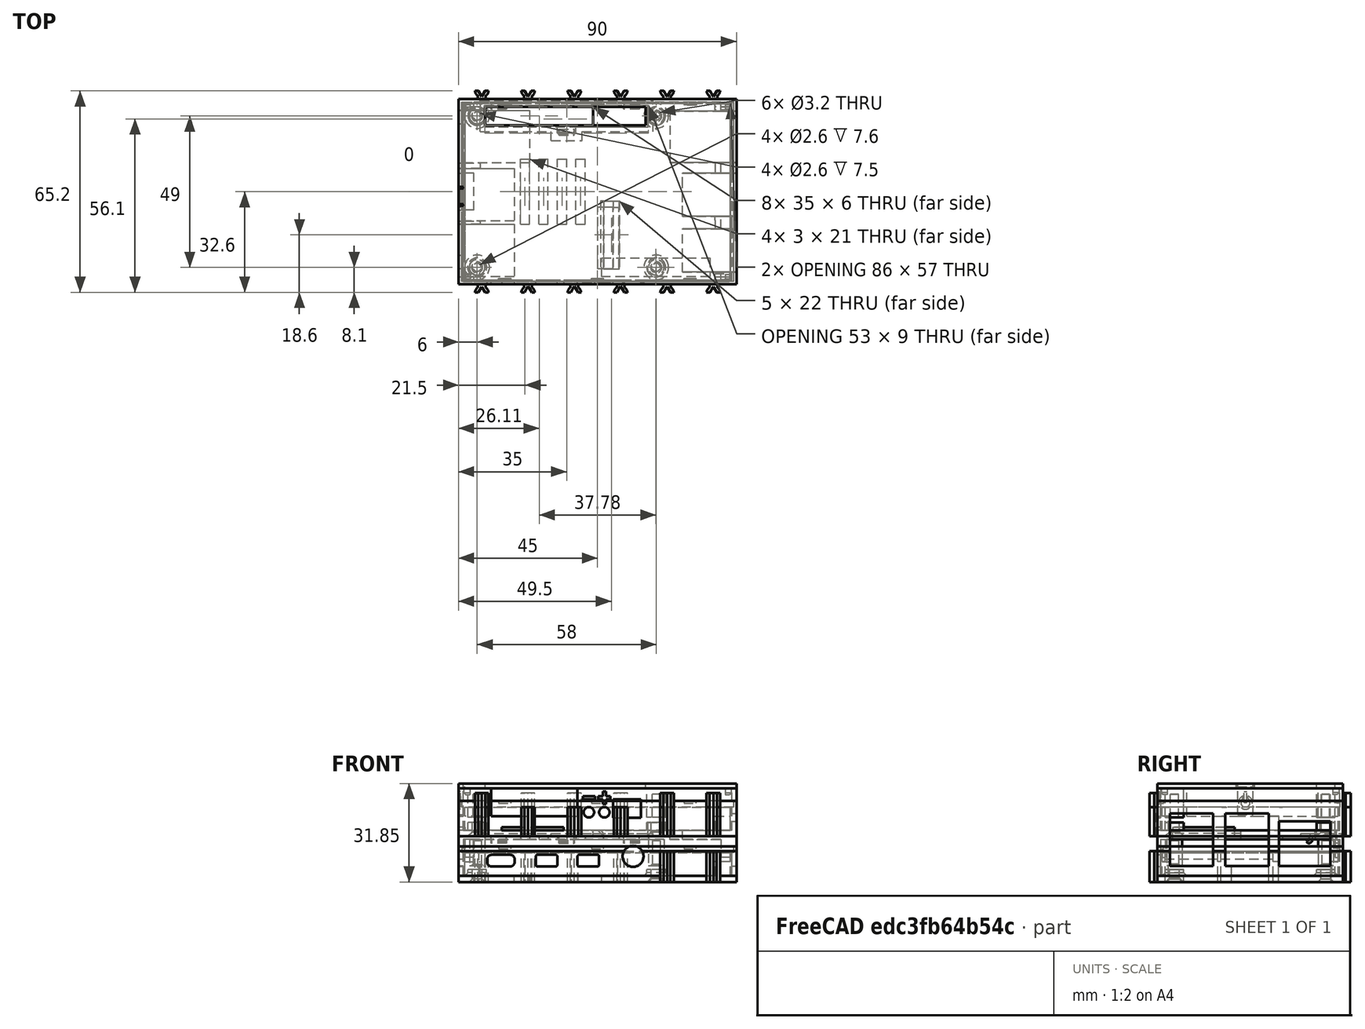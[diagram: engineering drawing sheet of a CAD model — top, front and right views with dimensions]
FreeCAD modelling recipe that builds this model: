
FCSTD DOCUMENT  (FreeCAD 0.19RUnknown)
Label: TX-Pi4_Case
License: All rights reserved
LicenseURL: http://en.wikipedia.org/wiki/All_rights_reserved
objects: Part::Box×86, Part::MultiFuse×79, Part::Cylinder×47, Part::Cut×28, Part::Extrusion×17, Sketcher::SketchObject×17, Part::Chamfer×16, Part::RegularPolygon×8, PartDesign::Pad×7, Part::Fillet×3, Part::Feature×1, PartDesign::Pocket×1, PartDesign::LinearPattern×1, PartDesign::Chamfer×1
note: 321 computed .brp shape members not serialized (recipe doc carries the construction recipe); baked Part::Feature solids carry a one-line shape summary decoded from their .brp

FEATURE [Part::Feature] RPi_4_dummy001
  Placement = pos=(-10,0,0) rot=(0,0,1;0rad)
  shape: bbox 90.5 x 58.5 x 18.2 mm, 1420 faces, 0 solids (baked)
FEATURE [Part::Box] Box  label="Aussen"
  AttacherType = Attacher::AttachEngine3D
  Height = 10
  Length = 90
  Placement = pos=(-45,-30,0) rot=(0,0,1;0rad)
  Width = 60
FEATURE [Part::Cylinder] Cylinder008  label="Audio"
  Angle = 360
  AttacherType = Attacher::AttachEngine3D
  Height = 10
  Placement = pos=(11.5,-23,8) rot=(1,0,0;1.5708rad)
  Radius = 3.4
FEATURE [Part::Cylinder] Cylinder001  label="Zylinder001"
  Angle = 360
  AttacherType = Attacher::AttachEngine3D
  Height = 10
  Placement = pos=(19,24.5,0) rot=(0,0,1;0rad)
  Radius = 1.6
FEATURE [Part::Box] Box001  label="Innen"
  AttacherType = Attacher::AttachEngine3D
  Height = 9.75
  Length = 87
  Placement = pos=(-43.5,-29,2) rot=(0,0,1;0rad)
  Width = 58
FEATURE [Part::Cylinder] Cylinder002  label="Zylinder002"
  Angle = 360
  AttacherType = Attacher::AttachEngine3D
  Height = 10
  Placement = pos=(19,24.5,0) rot=(0,0,1;0rad)
  Radius = 1.6
FEATURE [Part::Cut] Cut  label="Wanne roh"
  Base = -> Box
  Tool = -> Box001
FEATURE [Part::Cylinder] Cylinder  label="Zylinder"
  Angle = 360
  AttacherType = Attacher::AttachEngine3D
  Height = 10
  Placement = pos=(19,-24.5,0) rot=(0,0,1;0rad)
  Radius = 1.6
FEATURE [Part::MultiFuse] Fusion
  Shapes = -> [Cylinder,Cylinder001]
FEATURE [Part::Cylinder] Cylinder004  label="Zylinder004"
  Angle = 360
  AttacherType = Attacher::AttachEngine3D
  Height = 2
  Placement = pos=(19,24.5,0) rot=(0,0,1;0rad)
  Radius = 3
FEATURE [Part::Cylinder] Cylinder005  label="Zylinder005"
  Angle = 360
  AttacherType = Attacher::AttachEngine3D
  Height = 2
  Placement = pos=(19,24.5,0) rot=(0,0,1;0rad)
  Radius = 3
FEATURE [Part::Cylinder] Cylinder006  label="Zylinder006"
  Angle = 360
  AttacherType = Attacher::AttachEngine3D
  Height = 2
  Placement = pos=(19,-24.5,0) rot=(0,0,1;0rad)
  Radius = 3
FEATURE [Part::Cylinder] Cylinder003  label="Zylinder003"
  Angle = 360
  AttacherType = Attacher::AttachEngine3D
  Height = 10
  Placement = pos=(19,-24.5,0) rot=(0,0,1;0rad)
  Radius = 1.6
FEATURE [Part::MultiFuse] Fusion001
  Placement = pos=(-58,0,0) rot=(0,0,1;0rad)
  Shapes = -> [Cylinder003,Cylinder002]
FEATURE [Part::MultiFuse] Fusion002  label="Bohrungen"
  Placement = pos=(0,0,-5.3) rot=(0,0,1;0rad)
  Shapes = -> [Fusion001,Fusion]
FEATURE [Part::MultiFuse] Fusion003
  Shapes = -> [Cylinder006,Cylinder004]
FEATURE [Part::Cylinder] Cylinder007  label="Zylinder007"
  Angle = 360
  AttacherType = Attacher::AttachEngine3D
  Height = 2
  Placement = pos=(19,-24.5,0) rot=(0,0,1;0rad)
  Radius = 3
FEATURE [Part::MultiFuse] Fusion005
  Placement = pos=(-58,0,0) rot=(0,0,1;0rad)
  Shapes = -> [Cylinder007,Cylinder005]
FEATURE [Part::MultiFuse] Fusion004  label="Stützen"
  Placement = pos=(0,0,2) rot=(0,0,1;0rad)
  Shapes = -> [Fusion005,Fusion003]
FEATURE [Part::Box] Box002  label="SD-Slot"
  AttacherType = Attacher::AttachEngine3D
  Height = 6
  Length = 5
  Placement = pos=(-45,-6,-1) rot=(0,0,1;0rad)
  Width = 12
FEATURE [Part::Box] Box007  label="USB1"
  AttacherType = Attacher::AttachEngine3D
  Height = 16.6
  Length = 22
  Placement = pos=(27.5,-8,4.8) rot=(0,0,1;0rad)
  Width = 14
FEATURE [Part::Box] Box008  label="USB2"
  AttacherType = Attacher::AttachEngine3D
  Height = 16.6
  Length = 22
  Placement = pos=(27.5,-26,4.8) rot=(0,0,1;0rad)
  Width = 14
FEATURE [Part::Box] Box004  label="Würfel001"
  AttacherType = Attacher::AttachEngine3D
  Height = 3.8
  Length = 7
  Placement = pos=(-20,-29,4.7) rot=(0,0,1;0rad)
  Width = 10
FEATURE [Part::Box] Box006  label="Network"
  AttacherType = Attacher::AttachEngine3D
  Height = 14
  Length = 26
  Placement = pos=(23.5,9.4,4.8) rot=(0,0,1;0rad)
  Width = 16.6
FEATURE [Part::Box] Box005  label="Würfel002"
  AttacherType = Attacher::AttachEngine3D
  Height = 3.8
  Length = 7
  Placement = pos=(-20,-29,4.7) rot=(0,0,1;0rad)
  Width = 10
FEATURE [Part::Fillet] Fillet002  label="HDMI-2"
  Base = -> Box005
  Edges = 4 edges r=0.6: [Edge2,Edge4,Edge6,Edge8]
  Placement = pos=(13.5,-4,0) rot=(0,0,1;0rad)
FEATURE [Part::Box] Box003  label="Würfel"
  AttacherType = Attacher::AttachEngine3D
  Height = 3.8
  Length = 9
  Placement = pos=(-35.8,-29,4.7) rot=(0,0,1;0rad)
  Width = 10
FEATURE [Part::Fillet] Fillet  label="USB-C"
  Base = -> Box003
  Edges = 4 edges r=1.6: [Edge2,Edge4,Edge6,Edge8]
  Placement = pos=(0,-4,0) rot=(0,0,1;0rad)
FEATURE [Part::MultiFuse] Fusion007  label="Wanne mit Stuetzen"
  Shapes = -> [Cut,Fusion004]
FEATURE [Part::Fillet] Fillet001  label="HDMI-1"
  Base = -> Box004
  Edges = 4 edges r=0.6: [Edge2,Edge4,Edge6,Edge8]
  Placement = pos=(0,-4,0) rot=(0,0,1;0rad)
FEATURE [Part::MultiFuse] Fusion006  label="Aussparungen"
  Placement = pos=(0,0,0.3) rot=(0,0,1;0rad)
  Shapes = -> [Fusion002,Box002,Fillet,Fillet001,Fillet002,Cylinder008,Box006,Box007,Box008]
FEATURE [Part::Cut] Cut001  label="Wanne mit Aussparungen"
  Base = -> Fusion007
  Tool = -> Fusion006
FEATURE [Part::Chamfer] Chamfer002  label="Wanne Fasen innen"
  Base = -> Cut001
  Edges = 4 edges r=1: [Edge137,Edge138,Edge139,Edge140]
FEATURE [Part::Chamfer] Chamfer003  label="Wanne Fasen aussen"
  Base = -> Chamfer002
  Edges = 4 edges: [Edge96 r=1,Edge97 r=1.3,Edge98 r=1,Edge99 r=1]
FEATURE [Part::Box] Box026  label="Würfel017"
  AttacherType = Attacher::AttachEngine3D
  Height = 10
  Length = 5
  Placement = pos=(-40,-37.6,-3) rot=(0,0,1;0rad)
  Width = 5
FEATURE [Part::Box] Box035  label="Würfel026"
  AttacherType = Attacher::AttachEngine3D
  Height = 10
  Length = 2.5
  Placement = pos=(-38.75,-32.6,-3) rot=(0,0,1;0rad)
  Width = 2.6
FEATURE [Part::RegularPolygon] RegularPolygon005  label="Regelmäßiges Polygon005"
  AttacherType = Attacher::AttachEngine3D
  Circumradius = 2
  Placement = pos=(0,0,0) rot=(0,0,1;1.5708rad)
  Polygon = 3
FEATURE [Part::Cylinder] Cylinder018  label="Zylinder017"
  Angle = 360
  AttacherType = Attacher::AttachEngine3D
  Height = 10
  Placement = pos=(-37.5,-32.8,-3) rot=(0,0,1;0rad)
  Radius = 2.2
FEATURE [Part::Box] Box034  label="Würfel025"
  AttacherType = Attacher::AttachEngine3D
  Height = 10
  Length = 5
  Placement = pos=(-40,-37.6,-3) rot=(0,0,1;0rad)
  Width = 5
FEATURE [Part::Box] Box010  label="Würfel004"
  AttacherType = Attacher::AttachEngine3D
  Height = 3
  Length = 3
  Placement = pos=(10,-10.5,0) rot=(0,0,1;0rad)
  Width = 21
FEATURE [Part::Box] Box011  label="Deckel innen a"
  AttacherType = Attacher::AttachEngine3D
  Height = 10
  Length = 80
  Placement = pos=(-40,-29,1) rot=(0,0,1;0rad)
  Width = 58
FEATURE [Part::Cylinder] Cylinder012  label="Zylinder011"
  Angle = 360
  AttacherType = Attacher::AttachEngine3D
  Height = 8.5
  Placement = pos=(-19,24.5,1) rot=(0,0,1;0rad)
  Radius = 1.3
FEATURE [Part::Box] Box022  label="Würfel013"
  AttacherType = Attacher::AttachEngine3D
  Height = 10
  Length = 2.5
  Placement = pos=(-38.75,-32.6,-3) rot=(0,0,1;0rad)
  Width = 2.6
FEATURE [Part::Cylinder] Cylinder015  label="Zylinder014"
  Angle = 360
  AttacherType = Attacher::AttachEngine3D
  Height = 8.5
  Placement = pos=(-19,-24.5,1) rot=(0,0,1;0rad)
  Radius = 1.3
FEATURE [Part::Cylinder] Cylinder024  label="Zylinder023"
  Angle = 360
  AttacherType = Attacher::AttachEngine3D
  Height = 10
  Placement = pos=(-37.5,-32.8,-3) rot=(0,0,1;0rad)
  Radius = 2.2
FEATURE [Part::Cylinder] Cylinder013  label="Zylinder012"
  Angle = 360
  AttacherType = Attacher::AttachEngine3D
  Height = 8.5
  Placement = pos=(39,24.5,1) rot=(0,0,1;0rad)
  Radius = 1.3
FEATURE [Part::Cylinder] Cylinder016  label="Zylinder015"
  Angle = 360
  AttacherType = Attacher::AttachEngine3D
  Height = 8.5
  Placement = pos=(39,-24.5,1) rot=(0,0,1;0rad)
  Radius = 1.3
FEATURE [Part::Box] Box027  label="Würfel018"
  AttacherType = Attacher::AttachEngine3D
  Height = 10
  Length = 2.5
  Placement = pos=(-38.75,-32.6,-3) rot=(0,0,1;0rad)
  Width = 2.6
FEATURE [Part::MultiFuse] Fusion009  label="Schraubenbohrungen"
  Placement = pos=(0,0,0.4) rot=(0,0,1;0rad)
  Shapes = -> [Cylinder012,Cylinder013,Cylinder015,Cylinder016]
FEATURE [Part::Cylinder] Cylinder011  label="Zylinder010"
  Angle = 360
  AttacherType = Attacher::AttachEngine3D
  Height = 8.5
  Placement = pos=(-19,24.5,1) rot=(0,0,1;0rad)
  Radius = 2.5
FEATURE [Part::Box] Box021  label="Würfel012"
  AttacherType = Attacher::AttachEngine3D
  Height = 10
  Length = 53
  Placement = pos=(-16.5,21,0) rot=(0,0,1;0rad)
  Width = 7
FEATURE [Part::Box] Box018  label="Würfel005"
  AttacherType = Attacher::AttachEngine3D
  Height = 6.75
  Length = 3
  Placement = pos=(40,27.5,0) rot=(0,0,1;0rad)
  Width = 1
FEATURE [Part::Cylinder] Cylinder010  label="Zylinder009"
  Angle = 360
  AttacherType = Attacher::AttachEngine3D
  Height = 8.5
  Placement = pos=(39,-24.5,1) rot=(0,0,1;0rad)
  Radius = 2.5
FEATURE [Part::Box] Box009  label="Würfel003"
  AttacherType = Attacher::AttachEngine3D
  Height = 3
  Length = 3
  Placement = pos=(4,-10.5,0) rot=(0,0,1;0rad)
  Width = 21
FEATURE [Part::Box] Box013  label="Würfel007"
  AttacherType = Attacher::AttachEngine3D
  Height = 6.75
  Length = 3
  Placement = pos=(40,-28.5,0) rot=(0,0,1;0rad)
  Width = 1
FEATURE [Part::Cylinder] Cylinder009  label="Zylinder008"
  Angle = 360
  AttacherType = Attacher::AttachEngine3D
  Height = 8.5
  Placement = pos=(-19,-24.5,1) rot=(0,0,1;0rad)
  Radius = 2.5
FEATURE [Part::Box] Box017  label="Würfel011"
  AttacherType = Attacher::AttachEngine3D
  Height = 3
  Length = 3
  Placement = pos=(16,-10.5,0) rot=(0,0,1;0rad)
  Width = 21
FEATURE [Part::Box] Box019  label="Deckel aussen"
  AttacherType = Attacher::AttachEngine3D
  Height = 4.75
  Length = 90
  Placement = pos=(-45,-30,0) rot=(0,0,1;0rad)
  Width = 60
FEATURE [Part::Box] Box012  label="Würfel006"
  AttacherType = Attacher::AttachEngine3D
  Height = 6.75
  Length = 3
  Placement = pos=(-43,27.5,0) rot=(0,0,1;0rad)
  Width = 1
FEATURE [Part::Box] Box016  label="Würfel010"
  AttacherType = Attacher::AttachEngine3D
  Height = 3
  Length = 3
  Placement = pos=(22,-10.5,0) rot=(0,0,1;0rad)
  Width = 21
FEATURE [Part::MultiFuse] Fusion010  label="Lueftung"
  Shapes = -> [Box010,Box017,Box009,Box016]
FEATURE [Part::Box] Box015  label="Würfel009"
  AttacherType = Attacher::AttachEngine3D
  Height = 6.75
  Length = 3
  Placement = pos=(-43,-28.5,0) rot=(0,0,1;0rad)
  Width = 1
FEATURE [Part::MultiFuse] Fusion012  label="Zentrierung"
  Shapes = -> [Box015,Box018,Box012,Box013]
FEATURE [Part::Cylinder] Cylinder014  label="Zylinder013"
  Angle = 360
  AttacherType = Attacher::AttachEngine3D
  Height = 8.5
  Placement = pos=(39,24.5,1) rot=(0,0,1;0rad)
  Radius = 2.5
FEATURE [Part::MultiFuse] Fusion008  label="Stuetzen"
  Shapes = -> [Cylinder011,Cylinder014,Cylinder009,Cylinder010]
FEATURE [Part::Box] Box014  label="Würfel008"
  AttacherType = Attacher::AttachEngine3D
  Height = 10
  Length = 6
  Placement = pos=(7,19,0) rot=(0,0,1;0rad)
  Width = 2
FEATURE [Part::Box] Box020  label="Deckel innen b"
  AttacherType = Attacher::AttachEngine3D
  Height = 10
  Length = 3.5
  Placement = pos=(40,-27.5,1) rot=(0,0,1;0rad)
  Width = 56
FEATURE [Part::MultiFuse] Fusion015  label="Deckel innen"
  Shapes = -> [Box011,Box020]
FEATURE [Part::Cut] Cut002  label="Deckel roh"
  Base = -> Box019
  Tool = -> Fusion015
FEATURE [Part::MultiFuse] Fusion013  label="Deckel mit Einbauten"
  Shapes = -> [Cut002,Fusion012,Fusion008]
FEATURE [Part::MultiFuse] Fusion011  label="GPIO-Leiste"
  Shapes = -> [Box014,Box021]
FEATURE [Part::MultiFuse] Fusion014  label="Deckelaussparungen 1"
  Shapes = -> [Fusion009,Fusion010,Fusion011]
FEATURE [Part::Cut] Cut003  label="Deckel mit Aussparungen 1"
  Base = -> Fusion013
  Placement = pos=(0,0,14.75) rot=(0,1,0;3.14159rad)
  Tool = -> Fusion014
FEATURE [Part::Cut] Cut004  label="Deckel mit Aussparungen 2"
  Base = -> Cut003
  Tool = -> Fusion006
FEATURE [Part::RegularPolygon] RegularPolygon006  label="Regelmäßiges Polygon006"
  AttacherType = Attacher::AttachEngine3D
  Circumradius = 2
  Placement = pos=(0,0,0) rot=(0,0,1;1.5708rad)
  Polygon = 3
FEATURE [Part::Box] Box037  label="Würfel028"
  AttacherType = Attacher::AttachEngine3D
  Height = 10
  Length = 5
  Placement = pos=(-40,-37.6,-3) rot=(0,0,1;0rad)
  Width = 5
FEATURE [Part::Box] Box033  label="Würfel024"
  AttacherType = Attacher::AttachEngine3D
  Height = 10
  Length = 2.5
  Placement = pos=(-38.75,-32.6,-3) rot=(0,0,1;0rad)
  Width = 2.6
FEATURE [Part::Box] Box025  label="Würfel016"
  AttacherType = Attacher::AttachEngine3D
  Height = 10
  Length = 5
  Placement = pos=(-40,-37.6,-3) rot=(0,0,1;0rad)
  Width = 5
FEATURE [Part::Box] Box032  label="Würfel023"
  AttacherType = Attacher::AttachEngine3D
  Height = 10
  Length = 5
  Placement = pos=(-40,-37.6,-3) rot=(0,0,1;0rad)
  Width = 5
FEATURE [Part::Box] Box030  label="Würfel021"
  AttacherType = Attacher::AttachEngine3D
  Height = 10
  Length = 5
  Placement = pos=(-40,-37.6,-3) rot=(0,0,1;0rad)
  Width = 5
FEATURE [Part::Cylinder] Cylinder021  label="Zylinder020"
  Angle = 360
  AttacherType = Attacher::AttachEngine3D
  Height = 10
  Placement = pos=(-37.5,-32.8,-3) rot=(0,0,1;0rad)
  Radius = 2.2
FEATURE [Part::RegularPolygon] RegularPolygon  label="Regelmäßiges Polygon"
  AttacherType = Attacher::AttachEngine3D
  Circumradius = 2
  Placement = pos=(0,0,0) rot=(0,0,1;1.5708rad)
  Polygon = 3
FEATURE [Part::Extrusion] Extrude
  Base = -> RegularPolygon
  Dir = (0,0,1)
  DirMode = 2
  FaceMakerClass = Part::FaceMakerBullseye
  LengthFwd = 10
  LengthRev = 0
  Placement = pos=(-37.5,-32.8,-3) rot=(0,0,1;0rad)
  Solid = true
  Symmetric = false
FEATURE [Part::Cylinder] Cylinder023  label="Zylinder022"
  Angle = 360
  AttacherType = Attacher::AttachEngine3D
  Height = 10
  Placement = pos=(-37.5,-32.8,-3) rot=(0,0,1;0rad)
  Radius = 2.2
FEATURE [Part::MultiFuse] Fusion028
  Placement = pos=(0,0,3) rot=(0,0,1;0rad)
  Shapes = -> [Cylinder023,Box035]
FEATURE [Part::Box] Box031  label="Würfel022"
  AttacherType = Attacher::AttachEngine3D
  Height = 10
  Length = 2.5
  Placement = pos=(-38.75,-32.6,-3) rot=(0,0,1;0rad)
  Width = 2.6
FEATURE [Part::MultiFuse] Fusion024
  Placement = pos=(0,0,3) rot=(0,0,1;0rad)
  Shapes = -> [Cylinder021,Box031]
FEATURE [Part::Cylinder] Cylinder019  label="Zylinder018"
  Angle = 360
  AttacherType = Attacher::AttachEngine3D
  Height = 10
  Placement = pos=(-37.5,-32.8,-3) rot=(0,0,1;0rad)
  Radius = 2.2
FEATURE [Part::Chamfer] Chamfer004  label="Deckel Fasen"
  Base = -> Cut004
  Edges = 4 edges r=0.5: [Edge269,Edge270,Edge273,Edge274]
FEATURE [Part::Extrusion] Extrude005
  Base = -> RegularPolygon005
  Dir = (0,0,1)
  DirMode = 2
  FaceMakerClass = Part::FaceMakerBullseye
  LengthFwd = 10
  LengthRev = 0
  Placement = pos=(-37.5,-32.8,-3) rot=(0,0,1;0rad)
  Solid = true
  Symmetric = false
FEATURE [Part::RegularPolygon] RegularPolygon002  label="Regelmäßiges Polygon002"
  AttacherType = Attacher::AttachEngine3D
  Circumradius = 2
  Placement = pos=(0,0,0) rot=(0,0,1;1.5708rad)
  Polygon = 3
FEATURE [Part::Extrusion] Extrude002
  Base = -> RegularPolygon002
  Dir = (0,0,1)
  DirMode = 2
  FaceMakerClass = Part::FaceMakerBullseye
  LengthFwd = 10
  LengthRev = 0
  Placement = pos=(-37.5,-32.8,-3) rot=(0,0,1;0rad)
  Solid = true
  Symmetric = false
FEATURE [Part::Box] Box023  label="Würfel014"
  AttacherType = Attacher::AttachEngine3D
  Height = 10
  Length = 5
  Placement = pos=(-40,-37.6,-3) rot=(0,0,1;0rad)
  Width = 5
FEATURE [Part::MultiFuse] Fusion017
  Placement = pos=(0,0,3) rot=(0,0,1;0rad)
  Shapes = -> [Extrude,Box023]
FEATURE [Part::Box] Box024  label="Würfel015"
  AttacherType = Attacher::AttachEngine3D
  Height = 10
  Length = 2.5
  Placement = pos=(-38.75,-32.6,-3) rot=(0,0,1;0rad)
  Width = 2.6
FEATURE [Part::MultiFuse] Fusion019
  Placement = pos=(0,0,3) rot=(0,0,1;0rad)
  Shapes = -> [Cylinder018,Box024]
FEATURE [Part::Box] Box029  label="Würfel020"
  AttacherType = Attacher::AttachEngine3D
  Height = 10
  Length = 2.5
  Placement = pos=(-38.75,-32.6,-3) rot=(0,0,1;0rad)
  Width = 2.6
FEATURE [Part::MultiFuse] Fusion020
  Placement = pos=(0,0,3) rot=(0,0,1;0rad)
  Shapes = -> [Cylinder019,Box027]
FEATURE [Part::Box] Box036  label="Würfel027"
  AttacherType = Attacher::AttachEngine3D
  Height = 10
  Length = 2.5
  Placement = pos=(-38.75,-32.6,-3) rot=(0,0,1;0rad)
  Width = 2.6
FEATURE [Part::RegularPolygon] RegularPolygon004  label="Regelmäßiges Polygon004"
  AttacherType = Attacher::AttachEngine3D
  Circumradius = 2
  Placement = pos=(0,0,0) rot=(0,0,1;1.5708rad)
  Polygon = 3
FEATURE [Part::Extrusion] Extrude004
  Base = -> RegularPolygon004
  Dir = (0,0,1)
  DirMode = 2
  FaceMakerClass = Part::FaceMakerBullseye
  LengthFwd = 10
  LengthRev = 0
  Placement = pos=(-37.5,-32.8,-3) rot=(0,0,1;0rad)
  Solid = true
  Symmetric = false
FEATURE [Part::MultiFuse] Fusion025
  Placement = pos=(0,0,3) rot=(0,0,1;0rad)
  Shapes = -> [Extrude004,Box030]
FEATURE [Part::Cut] Cut009  label="ft-Feder004"
  Base = -> Fusion024
  Placement = pos=(-30,0,0) rot=(0,0,1;3.14159rad)
  Tool = -> Fusion025
FEATURE [Part::MultiFuse] Fusion032
  Placement = pos=(0,0,3) rot=(0,0,1;0rad)
  Shapes = -> [Cylinder024,Box036]
FEATURE [Part::MultiFuse] Fusion021
  Placement = pos=(0,0,3) rot=(0,0,1;0rad)
  Shapes = -> [Extrude002,Box026]
FEATURE [Part::Cut] Cut007  label="ft-Feder002"
  Base = -> Fusion020
  Placement = pos=(-60,0,0) rot=(0,0,1;3.14159rad)
  Tool = -> Fusion021
FEATURE [Part::Cylinder] Cylinder022  label="Zylinder021"
  Angle = 360
  AttacherType = Attacher::AttachEngine3D
  Height = 10
  Placement = pos=(-37.5,-32.8,-3) rot=(0,0,1;0rad)
  Radius = 2.2
FEATURE [Part::MultiFuse] Fusion026
  Placement = pos=(0,0,3) rot=(0,0,1;0rad)
  Shapes = -> [Cylinder022,Box033]
FEATURE [Part::Extrusion] Extrude006
  Base = -> RegularPolygon006
  Dir = (0,0,1)
  DirMode = 2
  FaceMakerClass = Part::FaceMakerBullseye
  LengthFwd = 10
  LengthRev = 0
  Placement = pos=(-37.5,-32.8,-3) rot=(0,0,1;0rad)
  Solid = true
  Symmetric = false
FEATURE [Part::MultiFuse] Fusion029
  Placement = pos=(0,0,3) rot=(0,0,1;0rad)
  Shapes = -> [Extrude006,Box034]
FEATURE [Part::Cut] Cut011  label="ft-Feder006"
  Base = -> Fusion028
  Placement = pos=(0,0,0) rot=(0,0,1;3.14159rad)
  Tool = -> Fusion029
FEATURE [Part::MultiFuse] Fusion027
  Placement = pos=(0,0,3) rot=(0,0,1;0rad)
  Shapes = -> [Extrude005,Box032]
FEATURE [Part::Cut] Cut010  label="ft-Feder005"
  Base = -> Fusion026
  Placement = pos=(-15,0,0) rot=(0,0,1;3.14159rad)
  Tool = -> Fusion027
FEATURE [Part::Box] Box028  label="Würfel019"
  AttacherType = Attacher::AttachEngine3D
  Height = 10
  Length = 5
  Placement = pos=(-40,-37.6,-3) rot=(0,0,1;0rad)
  Width = 5
FEATURE [Part::Cylinder] Cylinder020  label="Zylinder019"
  Angle = 360
  AttacherType = Attacher::AttachEngine3D
  Height = 10
  Placement = pos=(-37.5,-32.8,-3) rot=(0,0,1;0rad)
  Radius = 2.2
FEATURE [Part::MultiFuse] Fusion022
  Placement = pos=(0,0,3) rot=(0,0,1;0rad)
  Shapes = -> [Cylinder020,Box029]
FEATURE [Part::RegularPolygon] RegularPolygon007  label="Regelmäßiges Polygon007"
  AttacherType = Attacher::AttachEngine3D
  Circumradius = 2
  Placement = pos=(0,0,0) rot=(0,0,1;1.5708rad)
  Polygon = 3
FEATURE [Part::Extrusion] Extrude007
  Base = -> RegularPolygon007
  Dir = (0,0,1)
  DirMode = 2
  FaceMakerClass = Part::FaceMakerBullseye
  LengthFwd = 10
  LengthRev = 0
  Placement = pos=(-37.5,-32.8,-3) rot=(0,0,1;0rad)
  Solid = true
  Symmetric = false
FEATURE [Part::MultiFuse] Fusion031
  Placement = pos=(0,0,3) rot=(0,0,1;0rad)
  Shapes = -> [Extrude007,Box037]
FEATURE [Part::Cut] Cut012  label="ft-Feder007"
  Base = -> Fusion032
  Placement = pos=(15,0,0) rot=(0,0,1;0rad)
  Tool = -> Fusion031
FEATURE [Part::RegularPolygon] RegularPolygon001  label="Regelmäßiges Polygon001"
  AttacherType = Attacher::AttachEngine3D
  Circumradius = 2
  Placement = pos=(0,0,0) rot=(0,0,1;1.5708rad)
  Polygon = 3
FEATURE [Part::Extrusion] Extrude001
  Base = -> RegularPolygon001
  Dir = (0,0,1)
  DirMode = 2
  FaceMakerClass = Part::FaceMakerBullseye
  LengthFwd = 10
  LengthRev = 0
  Placement = pos=(-37.5,-32.8,-3) rot=(0,0,1;0rad)
  Solid = true
  Symmetric = false
FEATURE [Part::MultiFuse] Fusion018
  Placement = pos=(0,0,3) rot=(0,0,1;0rad)
  Shapes = -> [Extrude001,Box025]
FEATURE [Part::Cut] Cut006  label="ft-Feder001"
  Base = -> Fusion019
  Placement = pos=(-75,0,0) rot=(0,0,1;3.14159rad)
  Tool = -> Fusion018
FEATURE [Part::RegularPolygon] RegularPolygon003  label="Regelmäßiges Polygon003"
  AttacherType = Attacher::AttachEngine3D
  Circumradius = 2
  Placement = pos=(0,0,0) rot=(0,0,1;1.5708rad)
  Polygon = 3
FEATURE [Part::Extrusion] Extrude003
  Base = -> RegularPolygon003
  Dir = (0,0,1)
  DirMode = 2
  FaceMakerClass = Part::FaceMakerBullseye
  LengthFwd = 10
  LengthRev = 0
  Placement = pos=(-37.5,-32.8,-3) rot=(0,0,1;0rad)
  Solid = true
  Symmetric = false
FEATURE [Part::MultiFuse] Fusion023
  Placement = pos=(0,0,3) rot=(0,0,1;0rad)
  Shapes = -> [Extrude003,Box028]
FEATURE [Part::Cut] Cut008  label="ft-Feder003"
  Base = -> Fusion022
  Placement = pos=(-45,0,0) rot=(0,0,1;3.14159rad)
  Tool = -> Fusion023
FEATURE [Part::MultiFuse] Fusion030  label="ft-Federn links"
  Shapes = -> [Cut006,Cut007,Cut008,Cut009,Cut010,Cut011]
FEATURE [Part::Cylinder] Cylinder017  label="Zylinder016"
  Angle = 360
  AttacherType = Attacher::AttachEngine3D
  Height = 10
  Placement = pos=(-37.5,-32.8,-3) rot=(0,0,1;0rad)
  Radius = 2.2
FEATURE [Part::MultiFuse] Fusion016
  Placement = pos=(0,0,3) rot=(0,0,1;0rad)
  Shapes = -> [Cylinder017,Box022]
FEATURE [Part::Cut] Cut005  label="ft-Feder"
  Base = -> Fusion016
  Tool = -> Fusion017
FEATURE [Part::MultiFuse] Fusion033  label="ft-Federn rechts"
  Placement = pos=(60,0,0) rot=(0,0,1;0rad)
  Shapes = -> [Cut005,Cut012]
FEATURE [Part::MultiFuse] Fusion034  label="TX-Pi Wanne mit Federn"
  Shapes = -> [Chamfer003,Fusion030,Fusion033]
FEATURE [Sketcher::SketchObject] Sketch016
  MapMode = 5
  Placement = pos=(0,0,0) rot=(1,0,0;3.14159rad)
  sketch-geometry (13):
    g0: GeomPoint [constr] X=-37.5 Y=30 Z=0
    g1: LineSegment StartX=-38.75 StartY=30 StartZ=0 EndX=-36.25 EndY=30 EndZ=0
    g2: LineSegment StartX=-38.75 StartY=30 StartZ=0 EndX=-38.75 EndY=31 EndZ=0
    g3: LineSegment StartX=-36.25 StartY=30 StartZ=0 EndX=-36.25 EndY=31 EndZ=0
    g4: LineSegment [constr] StartX=-38.75 StartY=31 StartZ=0 EndX=-36.25 EndY=31 EndZ=0
    g5: ArcOfCircle CenterX=-37.5 CenterY=32.8104 CenterZ=0 NormalX=0 NormalY=0 NormalZ=1 AngleXU=0 Radius=2.2 StartAngle=3.23737 EndAngle=4.10809
    g6: ArcOfCircle CenterX=-37.5 CenterY=32.8104 CenterZ=0 NormalX=0 NormalY=0 NormalZ=1 AngleXU=0 Radius=2.2 StartAngle=5.31668 EndAngle=6.18741
    g7: LineSegment StartX=-39.6899 StartY=32.6 StartZ=0 EndX=-38.6899 EndY=32.6 EndZ=0
    g8: LineSegment StartX=-35.3101 StartY=32.6 StartZ=0 EndX=-36.3101 EndY=32.6 EndZ=0
    g9: LineSegment [constr] StartX=-38.6899 StartY=32.6 StartZ=0 EndX=-36.3101 EndY=32.6 EndZ=0
    g10: LineSegment StartX=-38.6899 StartY=32.6 StartZ=0 EndX=-37.5 EndY=30.8104 EndZ=0
    g11: LineSegment StartX=-37.5 StartY=30.8104 StartZ=0 EndX=-36.3101 EndY=32.6 EndZ=0
    g12: LineSegment [constr] StartX=-37.5 StartY=32.8104 StartZ=0 EndX=-37.5 EndY=30.8104 EndZ=0
  constraints (33):
    c: DistanceX(g0,g-1) = 37.5
    c: Symmetric(g1,g1,g0)
    c: DistanceX(g1,g1) = 2.5
    c: Vertical(g2)
    c: Vertical(g3)
    c: Coincident(g4,g2)
    c: Coincident(g4,g3)
    c: Coincident(g2,g1)
    c: Coincident(g1,g3)
    c: DistanceY(g1,g3) = 1
    c: Horizontal(g4)
    c: Coincident(g5,g2)
    c: Coincident(g6,g3)
    c: Radius(g5) = 2.2
    c: Equal(g5,g6)
    c: Coincident(g7,g5)
    c: Horizontal(g7)
    c: Coincident(g8,g6)
    c: Horizontal(g8)
    c: DistanceY(g1,g6) = 2.6
    c: DistanceX(g5,g7) = 1
    c: DistanceX(g8,g6) = 1
    c: Coincident(g9,g7)
    c: Coincident(g9,g8)
    c: Horizontal(g9)
    c: Coincident(g6,g5)
    c: Coincident(g10,g7)
    c: Coincident(g11,g8)
    c: Coincident(g10,g11)
    c: Coincident(g12,g5)
    c: Coincident(g12,g10)
    c: Vertical(g12)
    c: DistanceY(g10,g5) = 2
FEATURE [Sketcher::SketchObject] Sketch013
  MapMode = 5
  Placement = pos=(0,0,0) rot=(1,0,0;3.14159rad)
  sketch-geometry (13):
    g0: GeomPoint [constr] X=-37.5 Y=30 Z=0
    g1: LineSegment StartX=-38.75 StartY=30 StartZ=0 EndX=-36.25 EndY=30 EndZ=0
    g2: LineSegment StartX=-38.75 StartY=30 StartZ=0 EndX=-38.75 EndY=31 EndZ=0
    g3: LineSegment StartX=-36.25 StartY=30 StartZ=0 EndX=-36.25 EndY=31 EndZ=0
    g4: LineSegment [constr] StartX=-38.75 StartY=31 StartZ=0 EndX=-36.25 EndY=31 EndZ=0
    g5: ArcOfCircle CenterX=-37.5 CenterY=32.8104 CenterZ=0 NormalX=0 NormalY=0 NormalZ=1 AngleXU=0 Radius=2.2 StartAngle=3.23737 EndAngle=4.10809
    g6: ArcOfCircle CenterX=-37.5 CenterY=32.8104 CenterZ=0 NormalX=0 NormalY=0 NormalZ=1 AngleXU=0 Radius=2.2 StartAngle=5.31668 EndAngle=6.18741
    g7: LineSegment StartX=-39.6899 StartY=32.6 StartZ=0 EndX=-38.6899 EndY=32.6 EndZ=0
    g8: LineSegment StartX=-35.3101 StartY=32.6 StartZ=0 EndX=-36.3101 EndY=32.6 EndZ=0
    g9: LineSegment [constr] StartX=-38.6899 StartY=32.6 StartZ=0 EndX=-36.3101 EndY=32.6 EndZ=0
    g10: LineSegment StartX=-38.6899 StartY=32.6 StartZ=0 EndX=-37.5 EndY=30.8104 EndZ=0
    g11: LineSegment StartX=-37.5 StartY=30.8104 StartZ=0 EndX=-36.3101 EndY=32.6 EndZ=0
    g12: LineSegment [constr] StartX=-37.5 StartY=32.8104 StartZ=0 EndX=-37.5 EndY=30.8104 EndZ=0
  constraints (33):
    c: DistanceX(g0,g-1) = 37.5
    c: Symmetric(g1,g1,g0)
    c: DistanceX(g1,g1) = 2.5
    c: Vertical(g2)
    c: Vertical(g3)
    c: Coincident(g4,g2)
    c: Coincident(g4,g3)
    c: Coincident(g2,g1)
    c: Coincident(g1,g3)
    c: DistanceY(g1,g3) = 1
    c: Horizontal(g4)
    c: Coincident(g5,g2)
    c: Coincident(g6,g3)
    c: Radius(g5) = 2.2
    c: Equal(g5,g6)
    c: Coincident(g7,g5)
    c: Horizontal(g7)
    c: Coincident(g8,g6)
    c: Horizontal(g8)
    c: DistanceY(g1,g6) = 2.6
    c: DistanceX(g5,g7) = 1
    c: DistanceX(g8,g6) = 1
    c: Coincident(g9,g7)
    c: Coincident(g9,g8)
    c: Horizontal(g9)
    c: Coincident(g6,g5)
    c: Coincident(g10,g7)
    c: Coincident(g11,g8)
    c: Coincident(g10,g11)
    c: Coincident(g12,g5)
    c: Coincident(g12,g10)
    c: Vertical(g12)
    c: DistanceY(g10,g5) = 2
FEATURE [Sketcher::SketchObject] Sketch012
  MapMode = 5
  Placement = pos=(0,0,0) rot=(1,0,0;3.14159rad)
  sketch-geometry (13):
    g0: GeomPoint [constr] X=-37.5 Y=30 Z=0
    g1: LineSegment StartX=-38.75 StartY=30 StartZ=0 EndX=-36.25 EndY=30 EndZ=0
    g2: LineSegment StartX=-38.75 StartY=30 StartZ=0 EndX=-38.75 EndY=31 EndZ=0
    g3: LineSegment StartX=-36.25 StartY=30 StartZ=0 EndX=-36.25 EndY=31 EndZ=0
    g4: LineSegment [constr] StartX=-38.75 StartY=31 StartZ=0 EndX=-36.25 EndY=31 EndZ=0
    g5: ArcOfCircle CenterX=-37.5 CenterY=32.8104 CenterZ=0 NormalX=0 NormalY=0 NormalZ=1 AngleXU=0 Radius=2.2 StartAngle=3.23737 EndAngle=4.10809
    g6: ArcOfCircle CenterX=-37.5 CenterY=32.8104 CenterZ=0 NormalX=0 NormalY=0 NormalZ=1 AngleXU=0 Radius=2.2 StartAngle=5.31668 EndAngle=6.18741
    g7: LineSegment StartX=-39.6899 StartY=32.6 StartZ=0 EndX=-38.6899 EndY=32.6 EndZ=0
    g8: LineSegment StartX=-35.3101 StartY=32.6 StartZ=0 EndX=-36.3101 EndY=32.6 EndZ=0
    g9: LineSegment [constr] StartX=-38.6899 StartY=32.6 StartZ=0 EndX=-36.3101 EndY=32.6 EndZ=0
    g10: LineSegment StartX=-38.6899 StartY=32.6 StartZ=0 EndX=-37.5 EndY=30.8104 EndZ=0
    g11: LineSegment StartX=-37.5 StartY=30.8104 StartZ=0 EndX=-36.3101 EndY=32.6 EndZ=0
    g12: LineSegment [constr] StartX=-37.5 StartY=32.8104 StartZ=0 EndX=-37.5 EndY=30.8104 EndZ=0
  constraints (33):
    c: DistanceX(g0,g-1) = 37.5
    c: Symmetric(g1,g1,g0)
    c: DistanceX(g1,g1) = 2.5
    c: Vertical(g2)
    c: Vertical(g3)
    c: Coincident(g4,g2)
    c: Coincident(g4,g3)
    c: Coincident(g2,g1)
    c: Coincident(g1,g3)
    c: DistanceY(g1,g3) = 1
    c: Horizontal(g4)
    c: Coincident(g5,g2)
    c: Coincident(g6,g3)
    c: Radius(g5) = 2.2
    c: Equal(g5,g6)
    c: Coincident(g7,g5)
    c: Horizontal(g7)
    c: Coincident(g8,g6)
    c: Horizontal(g8)
    c: DistanceY(g1,g6) = 2.6
    c: DistanceX(g5,g7) = 1
    c: DistanceX(g8,g6) = 1
    c: Coincident(g9,g7)
    c: Coincident(g9,g8)
    c: Horizontal(g9)
    c: Coincident(g6,g5)
    c: Coincident(g10,g7)
    c: Coincident(g11,g8)
    c: Coincident(g10,g11)
    c: Coincident(g12,g5)
    c: Coincident(g12,g10)
    c: Vertical(g12)
    c: DistanceY(g10,g5) = 2
FEATURE [Sketcher::SketchObject] Sketch011
  MapMode = 5
  Placement = pos=(0,0,0) rot=(1,0,0;3.14159rad)
  sketch-geometry (13):
    g0: GeomPoint [constr] X=-37.5 Y=30 Z=0
    g1: LineSegment StartX=-38.75 StartY=30 StartZ=0 EndX=-36.25 EndY=30 EndZ=0
    g2: LineSegment StartX=-38.75 StartY=30 StartZ=0 EndX=-38.75 EndY=31 EndZ=0
    g3: LineSegment StartX=-36.25 StartY=30 StartZ=0 EndX=-36.25 EndY=31 EndZ=0
    g4: LineSegment [constr] StartX=-38.75 StartY=31 StartZ=0 EndX=-36.25 EndY=31 EndZ=0
    g5: ArcOfCircle CenterX=-37.5 CenterY=32.8104 CenterZ=0 NormalX=0 NormalY=0 NormalZ=1 AngleXU=0 Radius=2.2 StartAngle=3.23737 EndAngle=4.10809
    g6: ArcOfCircle CenterX=-37.5 CenterY=32.8104 CenterZ=0 NormalX=0 NormalY=0 NormalZ=1 AngleXU=0 Radius=2.2 StartAngle=5.31668 EndAngle=6.18741
    g7: LineSegment StartX=-39.6899 StartY=32.6 StartZ=0 EndX=-38.6899 EndY=32.6 EndZ=0
    g8: LineSegment StartX=-35.3101 StartY=32.6 StartZ=0 EndX=-36.3101 EndY=32.6 EndZ=0
    g9: LineSegment [constr] StartX=-38.6899 StartY=32.6 StartZ=0 EndX=-36.3101 EndY=32.6 EndZ=0
    g10: LineSegment StartX=-38.6899 StartY=32.6 StartZ=0 EndX=-37.5 EndY=30.8104 EndZ=0
    g11: LineSegment StartX=-37.5 StartY=30.8104 StartZ=0 EndX=-36.3101 EndY=32.6 EndZ=0
    g12: LineSegment [constr] StartX=-37.5 StartY=32.8104 StartZ=0 EndX=-37.5 EndY=30.8104 EndZ=0
  constraints (33):
    c: DistanceX(g0,g-1) = 37.5
    c: Symmetric(g1,g1,g0)
    c: DistanceX(g1,g1) = 2.5
    c: Vertical(g2)
    c: Vertical(g3)
    c: Coincident(g4,g2)
    c: Coincident(g4,g3)
    c: Coincident(g2,g1)
    c: Coincident(g1,g3)
    c: DistanceY(g1,g3) = 1
    c: Horizontal(g4)
    c: Coincident(g5,g2)
    c: Coincident(g6,g3)
    c: Radius(g5) = 2.2
    c: Equal(g5,g6)
    c: Coincident(g7,g5)
    c: Horizontal(g7)
    c: Coincident(g8,g6)
    c: Horizontal(g8)
    c: DistanceY(g1,g6) = 2.6
    c: DistanceX(g5,g7) = 1
    c: DistanceX(g8,g6) = 1
    c: Coincident(g9,g7)
    c: Coincident(g9,g8)
    c: Horizontal(g9)
    c: Coincident(g6,g5)
    c: Coincident(g10,g7)
    c: Coincident(g11,g8)
    c: Coincident(g10,g11)
    c: Coincident(g12,g5)
    c: Coincident(g12,g10)
    c: Vertical(g12)
    c: DistanceY(g10,g5) = 2
FEATURE [Sketcher::SketchObject] Sketch007
  MapMode = 5
  Placement = pos=(0,0,0) rot=(1,0,0;3.14159rad)
  sketch-geometry (13):
    g0: GeomPoint [constr] X=-37.5 Y=30 Z=0
    g1: LineSegment StartX=-38.75 StartY=30 StartZ=0 EndX=-36.25 EndY=30 EndZ=0
    g2: LineSegment StartX=-38.75 StartY=30 StartZ=0 EndX=-38.75 EndY=31 EndZ=0
    g3: LineSegment StartX=-36.25 StartY=30 StartZ=0 EndX=-36.25 EndY=31 EndZ=0
    g4: LineSegment [constr] StartX=-38.75 StartY=31 StartZ=0 EndX=-36.25 EndY=31 EndZ=0
    g5: ArcOfCircle CenterX=-37.5 CenterY=32.8104 CenterZ=0 NormalX=0 NormalY=0 NormalZ=1 AngleXU=0 Radius=2.2 StartAngle=3.23737 EndAngle=4.10809
    g6: ArcOfCircle CenterX=-37.5 CenterY=32.8104 CenterZ=0 NormalX=0 NormalY=0 NormalZ=1 AngleXU=0 Radius=2.2 StartAngle=5.31668 EndAngle=6.18741
    g7: LineSegment StartX=-39.6899 StartY=32.6 StartZ=0 EndX=-38.6899 EndY=32.6 EndZ=0
    g8: LineSegment StartX=-35.3101 StartY=32.6 StartZ=0 EndX=-36.3101 EndY=32.6 EndZ=0
    g9: LineSegment [constr] StartX=-38.6899 StartY=32.6 StartZ=0 EndX=-36.3101 EndY=32.6 EndZ=0
    g10: LineSegment StartX=-38.6899 StartY=32.6 StartZ=0 EndX=-37.5 EndY=30.8104 EndZ=0
    g11: LineSegment StartX=-37.5 StartY=30.8104 StartZ=0 EndX=-36.3101 EndY=32.6 EndZ=0
    g12: LineSegment [constr] StartX=-37.5 StartY=32.8104 StartZ=0 EndX=-37.5 EndY=30.8104 EndZ=0
  constraints (33):
    c: DistanceX(g0,g-1) = 37.5
    c: Symmetric(g1,g1,g0)
    c: DistanceX(g1,g1) = 2.5
    c: Vertical(g2)
    c: Vertical(g3)
    c: Coincident(g4,g2)
    c: Coincident(g4,g3)
    c: Coincident(g2,g1)
    c: Coincident(g1,g3)
    c: DistanceY(g1,g3) = 1
    c: Horizontal(g4)
    c: Coincident(g5,g2)
    c: Coincident(g6,g3)
    c: Radius(g5) = 2.2
    c: Equal(g5,g6)
    c: Coincident(g7,g5)
    c: Horizontal(g7)
    c: Coincident(g8,g6)
    c: Horizontal(g8)
    c: DistanceY(g1,g6) = 2.6
    c: DistanceX(g5,g7) = 1
    c: DistanceX(g8,g6) = 1
    c: Coincident(g9,g7)
    c: Coincident(g9,g8)
    c: Horizontal(g9)
    c: Coincident(g6,g5)
    c: Coincident(g10,g7)
    c: Coincident(g11,g8)
    c: Coincident(g10,g11)
    c: Coincident(g12,g5)
    c: Coincident(g12,g10)
    c: Vertical(g12)
    c: DistanceY(g10,g5) = 2
FEATURE [Part::Extrusion] Extrude009
  Base = -> Sketch007
  Dir = (0,0,1)
  DirMode = 0
  FaceMakerClass = Part::FaceMakerBullseye
  LengthFwd = 14
  LengthRev = 0
  Solid = true
  Symmetric = false
FEATURE [Part::Extrusion] Extrude010
  Base = -> Sketch011
  Dir = (0,0,1)
  DirMode = 0
  FaceMakerClass = Part::FaceMakerBullseye
  LengthFwd = 14
  LengthRev = 0
  Placement = pos=(60,0,0) rot=(0,0,1;0rad)
  Solid = true
  Symmetric = false
FEATURE [Part::Extrusion] Extrude012
  Base = -> Sketch013
  Dir = (0,0,1)
  DirMode = 0
  FaceMakerClass = Part::FaceMakerBullseye
  LengthFwd = 14
  LengthRev = 0
  Placement = pos=(0,0,0) rot=(0,0,1;3.14159rad)
  Solid = true
  Symmetric = false
FEATURE [Part::Extrusion] Extrude013
  Base = -> Sketch016
  Dir = (0,0,1)
  DirMode = 0
  FaceMakerClass = Part::FaceMakerBullseye
  LengthFwd = 14
  LengthRev = 0
  Placement = pos=(-75,0,0) rot=(0,0,1;3.14159rad)
  Solid = true
  Symmetric = false
FEATURE [Part::Box] Box038  label="Buchse 6-pol"
  AttacherType = Attacher::AttachEngine3D
  Height = 9
  Length = 10
  Placement = pos=(-45,-20.5,6.5) rot=(0,0,1;0rad)
  Width = 16
FEATURE [Part::Box] Box039  label="Buchse 10-pol001"
  AttacherType = Attacher::AttachEngine3D
  Height = 9
  Length = 10
  Placement = pos=(-45,1.5,6.5) rot=(0,0,1;0rad)
  Width = 20.5
FEATURE [Part::Box] Box040  label="Knopfloch"
  AttacherType = Attacher::AttachEngine3D
  Height = 9
  Length = 10
  Placement = pos=(-45,-4.5,6.5) rot=(0,0,1;0rad)
  Width = 6
FEATURE [Part::Box] Box041  label="Buchse 16-pol"
  AttacherType = Attacher::AttachEngine3D
  Height = 9
  Length = 28
  Placement = pos=(-34.5,-30,6.5) rot=(0,0,1;0rad)
  Width = 10
FEATURE [Part::Cylinder] Cylinder025  label="Zylinder024"
  Angle = 360
  AttacherType = Attacher::AttachEngine3D
  Height = 10
  Placement = pos=(-2.8,-20,7.8) rot=(1,0,0;1.5708rad)
  Radius = 1.7
FEATURE [Part::Cylinder] Cylinder026  label="Zylinder025"
  Angle = 360
  AttacherType = Attacher::AttachEngine3D
  Height = 10
  Placement = pos=(2.2,-20,7.8) rot=(1,0,0;1.5708rad)
  Radius = 1.7
FEATURE [Part::Box] Box042  label="Würfel029"
  AttacherType = Attacher::AttachEngine3D
  Height = 1
  Length = 4
  Placement = pos=(-4.8,-30,12) rot=(0,0,1;0rad)
  Width = 0.6
FEATURE [Part::Cylinder] Cylinder027  label="Zylinder026"
  Angle = 360
  AttacherType = Attacher::AttachEngine3D
  Height = 2.5
  Placement = pos=(-39,24.5,2) rot=(0,0,1;0rad)
  Radius = 3
FEATURE [Part::Cylinder] Cylinder028  label="Zylinder027"
  Angle = 360
  AttacherType = Attacher::AttachEngine3D
  Height = 4.5
  Placement = pos=(-39,24.5,0) rot=(0,0,1;0rad)
  Radius = 1.6
FEATURE [Sketcher::SketchObject] Sketch018
  MapMode = 5
  Placement = pos=(0,0,0) rot=(1,0,0;3.14159rad)
  sketch-geometry (13):
    g0: GeomPoint [constr] X=-37.5 Y=30 Z=0
    g1: LineSegment StartX=-38.75 StartY=30 StartZ=0 EndX=-36.25 EndY=30 EndZ=0
    g2: LineSegment StartX=-38.75 StartY=30 StartZ=0 EndX=-38.75 EndY=31 EndZ=0
    g3: LineSegment StartX=-36.25 StartY=30 StartZ=0 EndX=-36.25 EndY=31 EndZ=0
    g4: LineSegment [constr] StartX=-38.75 StartY=31 StartZ=0 EndX=-36.25 EndY=31 EndZ=0
    g5: ArcOfCircle CenterX=-37.5 CenterY=32.8104 CenterZ=0 NormalX=0 NormalY=0 NormalZ=1 AngleXU=0 Radius=2.2 StartAngle=3.23737 EndAngle=4.10809
    g6: ArcOfCircle CenterX=-37.5 CenterY=32.8104 CenterZ=0 NormalX=0 NormalY=0 NormalZ=1 AngleXU=0 Radius=2.2 StartAngle=5.31668 EndAngle=6.18741
    g7: LineSegment StartX=-39.6899 StartY=32.6 StartZ=0 EndX=-38.6899 EndY=32.6 EndZ=0
    g8: LineSegment StartX=-35.3101 StartY=32.6 StartZ=0 EndX=-36.3101 EndY=32.6 EndZ=0
    g9: LineSegment [constr] StartX=-38.6899 StartY=32.6 StartZ=0 EndX=-36.3101 EndY=32.6 EndZ=0
    g10: LineSegment StartX=-38.6899 StartY=32.6 StartZ=0 EndX=-37.5 EndY=30.8104 EndZ=0
    g11: LineSegment StartX=-37.5 StartY=30.8104 StartZ=0 EndX=-36.3101 EndY=32.6 EndZ=0
    g12: LineSegment [constr] StartX=-37.5 StartY=32.8104 StartZ=0 EndX=-37.5 EndY=30.8104 EndZ=0
  constraints (33):
    c: DistanceX(g0,g-1) = 37.5
    c: Symmetric(g1,g1,g0)
    c: DistanceX(g1,g1) = 2.5
    c: Vertical(g2)
    c: Vertical(g3)
    c: Coincident(g4,g2)
    c: Coincident(g4,g3)
    c: Coincident(g2,g1)
    c: Coincident(g1,g3)
    c: DistanceY(g1,g3) = 1
    c: Horizontal(g4)
    c: Coincident(g5,g2)
    c: Coincident(g6,g3)
    c: Radius(g5) = 2.2
    c: Equal(g5,g6)
    c: Coincident(g7,g5)
    c: Horizontal(g7)
    c: Coincident(g8,g6)
    c: Horizontal(g8)
    c: DistanceY(g1,g6) = 2.6
    c: DistanceX(g5,g7) = 1
    c: DistanceX(g8,g6) = 1
    c: Coincident(g9,g7)
    c: Coincident(g9,g8)
    c: Horizontal(g9)
    c: Coincident(g6,g5)
    c: Coincident(g10,g7)
    c: Coincident(g11,g8)
    c: Coincident(g10,g11)
    c: Coincident(g12,g5)
    c: Coincident(g12,g10)
    c: Vertical(g12)
    c: DistanceY(g10,g5) = 2
FEATURE [Part::Extrusion] Extrude008
  Base = -> Sketch018
  Dir = (0,0,1)
  DirMode = 0
  FaceMakerClass = Part::FaceMakerBullseye
  LengthFwd = 14
  LengthRev = 0
  Placement = pos=(-30,0,0) rot=(0,0,1;3.14159rad)
  Solid = true
  Symmetric = false
FEATURE [Part::Box] Box044  label="Würfel031"
  AttacherType = Attacher::AttachEngine3D
  Height = 5
  Length = 3
  Placement = pos=(-5,-27,-1) rot=(0,0,1;0rad)
  Width = 22
FEATURE [Part::Box] Box045  label="Würfel032"
  AttacherType = Attacher::AttachEngine3D
  Height = 1
  Length = 51
  Placement = pos=(-5,-25,-1) rot=(0,0,1;0rad)
  Width = 20
FEATURE [Part::MultiFuse] Fusion045  label="wire channel"
  Placement = pos=(0,-30,-1) rot=(0,0,1;3.14159rad)
  Shapes = -> [Box045,Box044]
FEATURE [Part::Box] Box046  label="Würfel033"
  AttacherType = Attacher::AttachEngine3D
  Height = 1
  Length = 51
  Placement = pos=(-5,-25,-1) rot=(0,0,1;0rad)
  Width = 20
FEATURE [Part::Cylinder] Cylinder029  label="Zylinder028"
  Angle = 360
  AttacherType = Attacher::AttachEngine3D
  Height = 2.5
  Placement = pos=(-39,-24.5,2) rot=(0,0,1;0rad)
  Radius = 3
FEATURE [Part::Cylinder] Cylinder030  label="Zylinder029"
  Angle = 360
  AttacherType = Attacher::AttachEngine3D
  Height = 4.5
  Placement = pos=(-39,-24.5,0) rot=(0,0,1;0rad)
  Radius = 1.6
FEATURE [Sketcher::SketchObject] Sketch017
  MapMode = 5
  Placement = pos=(0,0,0) rot=(1,0,0;3.14159rad)
  sketch-geometry (13):
    g0: GeomPoint [constr] X=-37.5 Y=30 Z=0
    g1: LineSegment StartX=-38.75 StartY=30 StartZ=0 EndX=-36.25 EndY=30 EndZ=0
    g2: LineSegment StartX=-38.75 StartY=30 StartZ=0 EndX=-38.75 EndY=31 EndZ=0
    g3: LineSegment StartX=-36.25 StartY=30 StartZ=0 EndX=-36.25 EndY=31 EndZ=0
    g4: LineSegment [constr] StartX=-38.75 StartY=31 StartZ=0 EndX=-36.25 EndY=31 EndZ=0
    g5: ArcOfCircle CenterX=-37.5 CenterY=32.8104 CenterZ=0 NormalX=0 NormalY=0 NormalZ=1 AngleXU=0 Radius=2.2 StartAngle=3.23737 EndAngle=4.10809
    g6: ArcOfCircle CenterX=-37.5 CenterY=32.8104 CenterZ=0 NormalX=0 NormalY=0 NormalZ=1 AngleXU=0 Radius=2.2 StartAngle=5.31668 EndAngle=6.18741
    g7: LineSegment StartX=-39.6899 StartY=32.6 StartZ=0 EndX=-38.6899 EndY=32.6 EndZ=0
    g8: LineSegment StartX=-35.3101 StartY=32.6 StartZ=0 EndX=-36.3101 EndY=32.6 EndZ=0
    g9: LineSegment [constr] StartX=-38.6899 StartY=32.6 StartZ=0 EndX=-36.3101 EndY=32.6 EndZ=0
    g10: LineSegment StartX=-38.6899 StartY=32.6 StartZ=0 EndX=-37.5 EndY=30.8104 EndZ=0
    g11: LineSegment StartX=-37.5 StartY=30.8104 StartZ=0 EndX=-36.3101 EndY=32.6 EndZ=0
    g12: LineSegment [constr] StartX=-37.5 StartY=32.8104 StartZ=0 EndX=-37.5 EndY=30.8104 EndZ=0
  constraints (33):
    c: DistanceX(g0,g-1) = 37.5
    c: Symmetric(g1,g1,g0)
    c: DistanceX(g1,g1) = 2.5
    c: Vertical(g2)
    c: Vertical(g3)
    c: Coincident(g4,g2)
    c: Coincident(g4,g3)
    c: Coincident(g2,g1)
    c: Coincident(g1,g3)
    c: DistanceY(g1,g3) = 1
    c: Horizontal(g4)
    c: Coincident(g5,g2)
    c: Coincident(g6,g3)
    c: Radius(g5) = 2.2
    c: Equal(g5,g6)
    c: Coincident(g7,g5)
    c: Horizontal(g7)
    c: Coincident(g8,g6)
    c: Horizontal(g8)
    c: DistanceY(g1,g6) = 2.6
    c: DistanceX(g5,g7) = 1
    c: DistanceX(g8,g6) = 1
    c: Coincident(g9,g7)
    c: Coincident(g9,g8)
    c: Horizontal(g9)
    c: Coincident(g6,g5)
    c: Coincident(g10,g7)
    c: Coincident(g11,g8)
    c: Coincident(g10,g11)
    c: Coincident(g12,g5)
    c: Coincident(g12,g10)
    c: Vertical(g12)
    c: DistanceY(g10,g5) = 2
FEATURE [Part::Cylinder] Cylinder031  label="Zylinder030"
  Angle = 360
  AttacherType = Attacher::AttachEngine3D
  Height = 4.5
  Placement = pos=(-39,24.5,0) rot=(0,0,1;0rad)
  Radius = 1.6
FEATURE [Part::Cylinder] Cylinder032  label="Zylinder031"
  Angle = 360
  AttacherType = Attacher::AttachEngine3D
  Height = 1.3
  Radius = 2.9
FEATURE [Part::Chamfer] Chamfer001  label="Ansenkung 4"
  Base = -> Cylinder032
  Edges = 1 edges r=1.29: [Edge1]
  Placement = pos=(-39,24.5,0) rot=(0,0,1;0rad)
FEATURE [Part::Box] Box047  label="Grundkoerper innen"
  AttacherType = Attacher::AttachEngine3D
  Height = 13.5
  Length = 87
  Placement = pos=(-43.5,-29,2) rot=(0,0,1;0rad)
  Width = 58
FEATURE [Part::Extrusion] Extrude015
  Base = -> Sketch012
  Dir = (0,0,1)
  DirMode = 0
  FaceMakerClass = Part::FaceMakerBullseye
  LengthFwd = 14
  LengthRev = 0
  Placement = pos=(75,0,0) rot=(0,0,1;0rad)
  Solid = true
  Symmetric = false
FEATURE [Part::Box] Box049  label="GPIO Header"
  AttacherType = Attacher::AttachEngine3D
  Height = 16
  Length = 53
  Placement = pos=(-36.61,21,0) rot=(0,0,1;0rad)
  Width = 7
FEATURE [Part::Box] Box050  label="Grundkoerper aussen"
  AttacherType = Attacher::AttachEngine3D
  Height = 15.5
  Length = 90
  Placement = pos=(-45,-30,0) rot=(0,0,1;0rad)
  Width = 60
FEATURE [Part::Cylinder] Cylinder033  label="Zylinder032"
  Angle = 360
  AttacherType = Attacher::AttachEngine3D
  Height = 2.5
  Placement = pos=(-39,-24.5,2) rot=(0,0,1;0rad)
  Radius = 3
FEATURE [Part::Cylinder] Cylinder034  label="Zylinder033"
  Angle = 360
  AttacherType = Attacher::AttachEngine3D
  Height = 2.5
  Placement = pos=(-39,24.5,2) rot=(0,0,1;0rad)
  Radius = 3
FEATURE [Part::MultiFuse] Fusion043
  Shapes = -> [Cylinder033,Cylinder034]
FEATURE [Sketcher::SketchObject] Sketch015
  MapMode = 5
  Placement = pos=(0,0,0) rot=(1,0,0;3.14159rad)
  sketch-geometry (13):
    g0: GeomPoint [constr] X=-37.5 Y=30 Z=0
    g1: LineSegment StartX=-38.75 StartY=30 StartZ=0 EndX=-36.25 EndY=30 EndZ=0
    g2: LineSegment StartX=-38.75 StartY=30 StartZ=0 EndX=-38.75 EndY=31 EndZ=0
    g3: LineSegment StartX=-36.25 StartY=30 StartZ=0 EndX=-36.25 EndY=31 EndZ=0
    g4: LineSegment [constr] StartX=-38.75 StartY=31 StartZ=0 EndX=-36.25 EndY=31 EndZ=0
    g5: ArcOfCircle CenterX=-37.5 CenterY=32.8104 CenterZ=0 NormalX=0 NormalY=0 NormalZ=1 AngleXU=0 Radius=2.2 StartAngle=3.23737 EndAngle=4.10809
    g6: ArcOfCircle CenterX=-37.5 CenterY=32.8104 CenterZ=0 NormalX=0 NormalY=0 NormalZ=1 AngleXU=0 Radius=2.2 StartAngle=5.31668 EndAngle=6.18741
    g7: LineSegment StartX=-39.6899 StartY=32.6 StartZ=0 EndX=-38.6899 EndY=32.6 EndZ=0
    g8: LineSegment StartX=-35.3101 StartY=32.6 StartZ=0 EndX=-36.3101 EndY=32.6 EndZ=0
    g9: LineSegment [constr] StartX=-38.6899 StartY=32.6 StartZ=0 EndX=-36.3101 EndY=32.6 EndZ=0
    g10: LineSegment StartX=-38.6899 StartY=32.6 StartZ=0 EndX=-37.5 EndY=30.8104 EndZ=0
    g11: LineSegment StartX=-37.5 StartY=30.8104 StartZ=0 EndX=-36.3101 EndY=32.6 EndZ=0
    g12: LineSegment [constr] StartX=-37.5 StartY=32.8104 StartZ=0 EndX=-37.5 EndY=30.8104 EndZ=0
  constraints (33):
    c: DistanceX(g0,g-1) = 37.5
    c: Symmetric(g1,g1,g0)
    c: DistanceX(g1,g1) = 2.5
    c: Vertical(g2)
    c: Vertical(g3)
    c: Coincident(g4,g2)
    c: Coincident(g4,g3)
    c: Coincident(g2,g1)
    c: Coincident(g1,g3)
    c: DistanceY(g1,g3) = 1
    c: Horizontal(g4)
    c: Coincident(g5,g2)
    c: Coincident(g6,g3)
    c: Radius(g5) = 2.2
    c: Equal(g5,g6)
    c: Coincident(g7,g5)
    c: Horizontal(g7)
    c: Coincident(g8,g6)
    c: Horizontal(g8)
    c: DistanceY(g1,g6) = 2.6
    c: DistanceX(g5,g7) = 1
    c: DistanceX(g8,g6) = 1
    c: Coincident(g9,g7)
    c: Coincident(g9,g8)
    c: Horizontal(g9)
    c: Coincident(g6,g5)
    c: Coincident(g10,g7)
    c: Coincident(g11,g8)
    c: Coincident(g10,g11)
    c: Coincident(g12,g5)
    c: Coincident(g12,g10)
    c: Vertical(g12)
    c: DistanceY(g10,g5) = 2
FEATURE [Part::Extrusion] Extrude014
  Base = -> Sketch015
  Dir = (0,0,1)
  DirMode = 0
  FaceMakerClass = Part::FaceMakerBullseye
  LengthFwd = 14
  LengthRev = 0
  Placement = pos=(-60,0,0) rot=(0,0,1;3.14159rad)
  Solid = true
  Symmetric = false
FEATURE [Part::MultiFuse] Fusion048
  Placement = pos=(58,0,0) rot=(0,0,1;0rad)
  Shapes = -> [Cylinder029,Cylinder027]
FEATURE [Part::MultiFuse] Fusion047  label="Stuetzen001"
  Shapes = -> [Fusion043,Fusion048]
FEATURE [Part::MultiFuse] Fusion050
  Shapes = -> [Cylinder030,Cylinder028]
FEATURE [Part::Cylinder] Cylinder035  label="Zylinder034"
  Angle = 360
  AttacherType = Attacher::AttachEngine3D
  Height = 4.5
  Placement = pos=(-39,-24.5,0) rot=(0,0,1;0rad)
  Radius = 1.6
FEATURE [Part::MultiFuse] Fusion042
  Placement = pos=(58,0,0) rot=(0,0,1;0rad)
  Shapes = -> [Cylinder035,Cylinder031]
FEATURE [Part::Extrusion] Extrude016
  Base = -> Sketch017
  Dir = (0,0,1)
  DirMode = 0
  FaceMakerClass = Part::FaceMakerBullseye
  LengthFwd = 14
  LengthRev = 0
  Placement = pos=(-45,0,0) rot=(0,0,1;3.14159rad)
  Solid = true
  Symmetric = false
FEATURE [Part::Cut] Cut017  label="Wanne roh 01"
  Base = -> Box050
  Tool = -> Box047
FEATURE [Part::MultiFuse] Fusion049  label="Wanne roh mit Stuetzen"
  Shapes = -> [Cut017,Fusion047]
FEATURE [Sketcher::SketchObject] Sketch014
  MapMode = 5
  Placement = pos=(0,0,0) rot=(1,0,0;3.14159rad)
  sketch-geometry (13):
    g0: GeomPoint [constr] X=-37.5 Y=30 Z=0
    g1: LineSegment StartX=-38.75 StartY=30 StartZ=0 EndX=-36.25 EndY=30 EndZ=0
    g2: LineSegment StartX=-38.75 StartY=30 StartZ=0 EndX=-38.75 EndY=31 EndZ=0
    g3: LineSegment StartX=-36.25 StartY=30 StartZ=0 EndX=-36.25 EndY=31 EndZ=0
    g4: LineSegment [constr] StartX=-38.75 StartY=31 StartZ=0 EndX=-36.25 EndY=31 EndZ=0
    g5: ArcOfCircle CenterX=-37.5 CenterY=32.8104 CenterZ=0 NormalX=0 NormalY=0 NormalZ=1 AngleXU=0 Radius=2.2 StartAngle=3.23737 EndAngle=4.10809
    g6: ArcOfCircle CenterX=-37.5 CenterY=32.8104 CenterZ=0 NormalX=0 NormalY=0 NormalZ=1 AngleXU=0 Radius=2.2 StartAngle=5.31668 EndAngle=6.18741
    g7: LineSegment StartX=-39.6899 StartY=32.6 StartZ=0 EndX=-38.6899 EndY=32.6 EndZ=0
    g8: LineSegment StartX=-35.3101 StartY=32.6 StartZ=0 EndX=-36.3101 EndY=32.6 EndZ=0
    g9: LineSegment [constr] StartX=-38.6899 StartY=32.6 StartZ=0 EndX=-36.3101 EndY=32.6 EndZ=0
    g10: LineSegment StartX=-38.6899 StartY=32.6 StartZ=0 EndX=-37.5 EndY=30.8104 EndZ=0
    g11: LineSegment StartX=-37.5 StartY=30.8104 StartZ=0 EndX=-36.3101 EndY=32.6 EndZ=0
    g12: LineSegment [constr] StartX=-37.5 StartY=32.8104 StartZ=0 EndX=-37.5 EndY=30.8104 EndZ=0
  constraints (33):
    c: DistanceX(g0,g-1) = 37.5
    c: Symmetric(g1,g1,g0)
    c: DistanceX(g1,g1) = 2.5
    c: Vertical(g2)
    c: Vertical(g3)
    c: Coincident(g4,g2)
    c: Coincident(g4,g3)
    c: Coincident(g2,g1)
    c: Coincident(g1,g3)
    c: DistanceY(g1,g3) = 1
    c: Horizontal(g4)
    c: Coincident(g5,g2)
    c: Coincident(g6,g3)
    c: Radius(g5) = 2.2
    c: Equal(g5,g6)
    c: Coincident(g7,g5)
    c: Horizontal(g7)
    c: Coincident(g8,g6)
    c: Horizontal(g8)
    c: DistanceY(g1,g6) = 2.6
    c: DistanceX(g5,g7) = 1
    c: DistanceX(g8,g6) = 1
    c: Coincident(g9,g7)
    c: Coincident(g9,g8)
    c: Horizontal(g9)
    c: Coincident(g6,g5)
    c: Coincident(g10,g7)
    c: Coincident(g11,g8)
    c: Coincident(g10,g11)
    c: Coincident(g12,g5)
    c: Coincident(g12,g10)
    c: Vertical(g12)
    c: DistanceY(g10,g5) = 2
FEATURE [Part::Extrusion] Extrude011
  Base = -> Sketch014
  Dir = (0,0,1)
  DirMode = 0
  FaceMakerClass = Part::FaceMakerBullseye
  LengthFwd = 14
  LengthRev = 0
  Placement = pos=(-15,0,0) rot=(0,0,1;3.14159rad)
  Solid = true
  Symmetric = false
FEATURE [Part::MultiFuse] Fusion044  label="Wannenfedern"
  Shapes = -> [Extrude009,Extrude010,Extrude015,Extrude011,Extrude012,Extrude008,Extrude014,Extrude016,Extrude013]
FEATURE [Part::MultiFuse] Fusion052  label="Bohrungen001"
  Shapes = -> [Fusion050,Fusion042]
FEATURE [Part::Box] Box052  label="Würfel037"
  AttacherType = Attacher::AttachEngine3D
  Height = 5
  Length = 3
  Placement = pos=(-5,-25,-1) rot=(0,0,1;0rad)
  Width = 20
FEATURE [Part::MultiFuse] Fusion046  label="wire channel001"
  Placement = pos=(-6,-30,3) rot=(0,0,-1;1.5708rad)
  Shapes = -> [Box046,Box052]
FEATURE [Part::MultiFuse] Fusion053  label="Bundhuelsen"
  Shapes = -> [Cylinder025,Cylinder026]
FEATURE [Part::Box] Box053  label="Würfel038"
  AttacherType = Attacher::AttachEngine3D
  Height = 1
  Length = 4
  Placement = pos=(0.2,-30,12) rot=(0,0,1;0rad)
  Width = 0.6
FEATURE [Part::Box] Box054  label="Würfel039"
  AttacherType = Attacher::AttachEngine3D
  Height = 1
  Length = 4
  Placement = pos=(1.7,-30,14.5) rot=(0,1,0;1.5708rad)
  Width = 0.6
FEATURE [Part::MultiFuse] Fusion054  label="PlusMinus"
  Shapes = -> [Box042,Box053,Box054]
FEATURE [Part::MultiFuse] Fusion055  label="ft-Bundhuelsen"
  Shapes = -> [Fusion053,Fusion054]
FEATURE [Part::Box] Box055  label="Powerbuchse"
  AttacherType = Attacher::AttachEngine3D
  Height = 6
  Length = 9
  Placement = pos=(5,-30,6) rot=(0,0,1;0rad)
  Width = 10
FEATURE [Part::MultiFuse] Fusion036  label="Wannenaussparungen"
  Shapes = -> [Box038,Box039,Box040,Box041,Fusion055,Box055]
FEATURE [Part::Box] Box056  label="Network001"
  AttacherType = Attacher::AttachEngine3D
  Height = 14
  Length = 26
  Placement = pos=(23.5,9.4,4.8) rot=(0,0,1;0rad)
  Width = 16.6
FEATURE [Part::Box] Box057  label="USB003"
  AttacherType = Attacher::AttachEngine3D
  Height = 16.6
  Length = 22
  Placement = pos=(27.5,-8,4.8) rot=(0,0,1;0rad)
  Width = 14
FEATURE [Part::Box] Box058  label="USB004"
  AttacherType = Attacher::AttachEngine3D
  Height = 16.6
  Length = 22
  Placement = pos=(27.5,-26,4.8) rot=(0,0,1;0rad)
  Width = 14
FEATURE [Part::MultiFuse] Fusion056  label="Rear USB & Network slots"
  Placement = pos=(0,0,-13.95) rot=(0,0,1;0rad)
  Shapes = -> [Box056,Box057,Box058]
FEATURE [Part::MultiFuse] Fusion057  label="Aussparungen 1"
  Shapes = -> [Box049,Fusion052]
FEATURE [Part::Cut] Cut018  label="Wanne geschnitten 1"
  Base = -> Fusion049
  Tool = -> Fusion057
FEATURE [Part::MultiFuse] Fusion058  label="Aussparungen Exp 2"
  Shapes = -> [Fusion036,Fusion045,Fusion046,Fusion056]
FEATURE [Part::Cut] Cut019  label="Wanne Aussparungen 2"
  Base = -> Cut018
  Tool = -> Fusion058
FEATURE [Part::MultiFuse] Fusion059  label="Expander Wanne mit Federn roh"
  Shapes = -> [Cut019,Fusion044]
FEATURE [Part::Cylinder] Cylinder036  label="Zylinder035"
  Angle = 360
  AttacherType = Attacher::AttachEngine3D
  Height = 1.3
  Radius = 2.9
FEATURE [Part::Chamfer] Chamfer005  label="Ansenkung 3"
  Base = -> Cylinder036
  Edges = 1 edges r=1.29: [Edge1]
  Placement = pos=(19,24.5,0) rot=(0,0,1;0rad)
FEATURE [Part::MultiFuse] Fusion060  label="Ansenkungen Exp-Wanne"
  Shapes = -> [Chamfer001,Chamfer005]
FEATURE [Part::Chamfer] Chamfer
  Base = -> Fusion059
  Edges = 2 edges r=1.5: [Edge86,Edge91]
FEATURE [Part::Cut] Cut020  label="Expander-Wanne"
  Base = -> Chamfer
  Tool = -> Fusion060
FEATURE [Part::Chamfer] Chamfer006  label="Expander-Wanne mit ribbon champfer"
  Base = -> Cut020
  Edges = 2 edges: [Edge38 r=1.9,Edge235 r=1]
  Placement = pos=(0,0,14.75) rot=(0,0,1;0rad)
FEATURE [Part::Box] Box059  label="Knopf"
  AttacherType = Attacher::AttachEngine3D
  Height = 8.5
  Length = 1.5
  Placement = pos=(-45,-4,7) rot=(0,0,1;0rad)
  Width = 5
FEATURE [Part::Box] Box060  label="Knopf001"
  AttacherType = Attacher::AttachEngine3D
  Height = 1
  Length = 0.5
  Placement = pos=(-43.5,-4.5,15) rot=(0,0,1;0rad)
  Width = 6
FEATURE [Part::Box] Box061  label="Knopf002"
  AttacherType = Attacher::AttachEngine3D
  Height = 3
  Length = 1.5
  Placement = pos=(-45,1,15) rot=(0,0,1;0rad)
  Width = 0.5
FEATURE [Part::Box] Box062  label="Würfel040"
  AttacherType = Attacher::AttachEngine3D
  Height = 2
  Length = 2
  Placement = pos=(41.3,26.8,14) rot=(0,0,1;0rad)
  Width = 2
FEATURE [Part::Cylinder] Cylinder037  label="Zylinder036"
  Angle = 360
  AttacherType = Attacher::AttachEngine3D
  Height = 8
  Placement = pos=(-39,-24.5,0) rot=(0,0,1;0rad)
  Radius = 1.3
FEATURE [Part::Box] Box063  label="Würfel041"
  AttacherType = Attacher::AttachEngine3D
  Height = 0.6
  Length = 4
  Placement = pos=(0,-0.8,0) rot=(0,0,1;0rad)
  Width = 1.6
FEATURE [Part::Box] Box064  label="On"
  AttacherType = Attacher::AttachEngine3D
  Height = 0.6
  Length = 3.6
  Placement = pos=(0,-0.4,0) rot=(0,0,1;0rad)
  Width = 0.8
FEATURE [Part::Cylinder] Cylinder038  label="Zylinder037"
  Angle = 360
  AttacherType = Attacher::AttachEngine3D
  Height = 9.5
  Placement = pos=(-39,-24.5,2) rot=(0,0,1;0rad)
  Radius = 3
FEATURE [Part::Box] Box065  label="Würfel042"
  AttacherType = Attacher::AttachEngine3D
  Height = 2
  Length = 2
  Placement = pos=(41.3,-28.8,14) rot=(0,0,1;0rad)
  Width = 2
FEATURE [Part::Cylinder] Cylinder039  label="Zylinder038"
  Angle = 360
  AttacherType = Attacher::AttachEngine3D
  Height = 9.5
  Placement = pos=(-39,-24.5,2) rot=(0,0,1;0rad)
  Radius = 3
FEATURE [Part::Cylinder] Cylinder040  label="Zylinder039"
  Angle = 360
  AttacherType = Attacher::AttachEngine3D
  Height = 8
  Placement = pos=(-39,-24.5,0) rot=(0,0,1;0rad)
  Radius = 1.3
FEATURE [Part::Cylinder] Cylinder041  label="Zylinder040"
  Angle = 360
  AttacherType = Attacher::AttachEngine3D
  Height = 9.5
  Placement = pos=(-39,24.5,2) rot=(0,0,1;0rad)
  Radius = 3
FEATURE [Part::Box] Box066  label="Knopf003"
  AttacherType = Attacher::AttachEngine3D
  Height = 3
  Length = 1.5
  Placement = pos=(-45,-4.5,15) rot=(0,0,1;0rad)
  Width = 0.5
FEATURE [Part::MultiFuse] Fusion038  label="Knopfaussparungen"
  Shapes = -> [Box060,Box061,Box066]
FEATURE [Part::Cylinder] Cylinder042  label="Zylinder041"
  Angle = 360
  AttacherType = Attacher::AttachEngine3D
  Height = 0.6
  Radius = 2.2
FEATURE [Part::Cylinder] Cylinder043  label="Zylinder042"
  Angle = 360
  AttacherType = Attacher::AttachEngine3D
  Height = 0.6
  Radius = 1.5
FEATURE [Part::Cut] Cut026
  Base = -> Cylinder042
  Tool = -> Cylinder043
FEATURE [Part::Cut] Cut023  label="Off"
  Base = -> Cut026
  Tool = -> Box063
FEATURE [Part::MultiFuse] Fusion040  label="OnOff"
  Placement = pos=(-44.4,-1.5,11) rot=(0,-1,0;1.5708rad)
  Shapes = -> [Box064,Cut023]
FEATURE [Part::Cylinder] Cylinder044  label="Zylinder043"
  Angle = 360
  AttacherType = Attacher::AttachEngine3D
  Height = 8
  Placement = pos=(-39,24.5,0) rot=(0,0,1;0rad)
  Radius = 1.3
FEATURE [Part::Cylinder] Cylinder045  label="Zylinder044"
  Angle = 360
  AttacherType = Attacher::AttachEngine3D
  Height = 8
  Placement = pos=(-39,24.5,0) rot=(0,0,1;0rad)
  Radius = 1.3
FEATURE [Part::MultiFuse] Fusion064
  Placement = pos=(58,0,0) rot=(0,0,1;0rad)
  Shapes = -> [Cylinder037,Cylinder045]
FEATURE [Part::Box] Box067  label="Würfel043"
  AttacherType = Attacher::AttachEngine3D
  Height = 2
  Length = 2
  Placement = pos=(41.3,26.8,14) rot=(0,0,1;0rad)
  Width = 2
FEATURE [Part::MultiFuse] Fusion061
  Shapes = -> [Box067,Box065]
FEATURE [Part::Cylinder] Cylinder046  label="Zylinder045"
  Angle = 360
  AttacherType = Attacher::AttachEngine3D
  Height = 9.5
  Placement = pos=(-39,24.5,2) rot=(0,0,1;0rad)
  Radius = 3
FEATURE [Part::MultiFuse] Fusion062
  Shapes = -> [Cylinder038,Cylinder046]
FEATURE [Part::MultiFuse] Fusion068
  Placement = pos=(58,0,0) rot=(0,0,1;0rad)
  Shapes = -> [Cylinder039,Cylinder041]
FEATURE [Part::MultiFuse] Fusion063  label="Stuetzen002"
  Placement = pos=(0,0,4.1) rot=(0,0,1;0rad)
  Shapes = -> [Fusion062,Fusion068]
FEATURE [Part::MultiFuse] Fusion070
  Shapes = -> [Cylinder040,Cylinder044]
FEATURE [Part::MultiFuse] Fusion069  label="Bohrungen002"
  Placement = pos=(0,0,5.6) rot=(0,0,1;0rad)
  Shapes = -> [Fusion070,Fusion064]
FEATURE [Part::Cut] Cut022  label="Deckelstützen"
  Base = -> Fusion063
  Tool = -> Fusion069
FEATURE [Part::Box] Box068  label="Stack-Öffnung"
  AttacherType = Attacher::AttachEngine3D
  Height = 12
  Length = 52
  Placement = pos=(-36.38,21.5,6) rot=(0,0,1;0rad)
  Width = 6
FEATURE [Part::Box] Box069  label="Deckel geom."
  AttacherType = Attacher::AttachEngine3D
  Height = 1.6
  Length = 90
  Placement = pos=(-45,-30,15.5) rot=(0,0,1;0rad)
  Width = 60
FEATURE [Part::MultiFuse] Fusion037  label="Deckel mit Stützen"
  Shapes = -> [Box069,Cut022]
FEATURE [Part::Cut] Cut021  label="Deckel mit Stacköffnung"
  Base = -> Fusion037
  Tool = -> Box068
FEATURE [Part::Cut] Cut025  label="Deckel mit Knopfschlitzen"
  Base = -> Cut021
  Tool = -> Fusion038
FEATURE [Part::MultiFuse] Fusion039  label="Deckel mit Knopf"
  Shapes = -> [Box059,Cut025]
FEATURE [Part::Cut] Cut024  label="Deckel mit IO-Button"
  Base = -> Fusion039
  Tool = -> Fusion040
FEATURE [Part::Box] Box070  label="Würfel044"
  AttacherType = Attacher::AttachEngine3D
  Height = 2
  Length = 2
  Placement = pos=(41.3,-28.8,14) rot=(0,0,1;0rad)
  Width = 2
FEATURE [Part::MultiFuse] Fusion066
  Placement = pos=(-84.6,0,0) rot=(0,0,1;0rad)
  Shapes = -> [Box062,Box070]
FEATURE [Part::MultiFuse] Fusion065
  Shapes = -> [Fusion061,Fusion066]
FEATURE [Part::Chamfer] Chamfer007  label="Zentrierer"
  Base = -> Fusion065
  Edges = 8 edges r=0.6: [Edge6,Edge12,Edge18,Edge22,Edge26,Edge36,Edge38,Edge46]
  Placement = pos=(0,0,29.5) rot=(1,0,0;3.14159rad)
FEATURE [Part::MultiFuse] Fusion067  label="Expander-Deckel fertig"
  Placement = pos=(0,0,14.75) rot=(0,0,1;0rad)
  Shapes = -> [Chamfer007,Cut024]
FEATURE [Part::Box] Box071  label="Würfel045"
  AttacherType = Attacher::AttachEngine3D
  Height = 10
  Length = 5
  Placement = pos=(2,-25,7) rot=(0,0,1;0rad)
  Width = 22
FEATURE [Part::Cut] Cut027  label="TX-Pi Deckel mit Ribbon slot"
  Base = -> Chamfer004
  Tool = -> Box071
FEATURE [Part::Box] Box072  label="Würfel046"
  AttacherType = Attacher::AttachEngine3D
  Height = 5
  Length = 3
  Placement = pos=(-5,-25,-1) rot=(0,0,1;0rad)
  Width = 20
FEATURE [Part::Box] Box073  label="Würfel047"
  AttacherType = Attacher::AttachEngine3D
  Height = 1
  Length = 51
  Placement = pos=(-5,-25,-1) rot=(0,0,1;0rad)
  Width = 20
FEATURE [Part::Box] Box074  label="Würfel048"
  AttacherType = Attacher::AttachEngine3D
  Height = 1
  Length = 51
  Placement = pos=(-5,-25,-1) rot=(0,0,1;0rad)
  Width = 20
FEATURE [Part::Box] Box075  label="Würfel049"
  AttacherType = Attacher::AttachEngine3D
  Height = 5
  Length = 3
  Placement = pos=(-5,-25,-1) rot=(0,0,1;0rad)
  Width = 20
FEATURE [Part::MultiFuse] Fusion073  label="wire channel003"
  Placement = pos=(0,30,3) rot=(0,0,1;0rad)
  Shapes = -> [Box074,Box075]
FEATURE [Part::MultiFuse] Fusion074  label="wire channel002"
  Placement = pos=(0,30,-1) rot=(0,0,1;0rad)
  Shapes = -> [Box073,Box072]
FEATURE [Sketcher::SketchObject] Sketch008
  MapMode = 5
  sketch-geometry (30):
    g0: LineSegment StartX=-45 StartY=30 StartZ=0 EndX=-45 EndY=26.25 EndZ=0
    g1: LineSegment StartX=-45 StartY=26.25 StartZ=0 EndX=-22 EndY=26.25 EndZ=0
    g2: LineSegment StartX=-22 StartY=26.25 StartZ=0 EndX=-22 EndY=9.25 EndZ=0
    g3: LineSegment StartX=-22 StartY=9.25 StartZ=0 EndX=-45 EndY=9.25 EndZ=0
    g4: LineSegment StartX=-45 StartY=9.25 StartZ=0 EndX=-45 EndY=7.5 EndZ=0
    g5: LineSegment StartX=-45 StartY=7.5 StartZ=0 EndX=-27 EndY=7.5 EndZ=0
    g6: LineSegment StartX=-27 StartY=7.5 StartZ=0 EndX=-27 EndY=-9.5 EndZ=0
    g7: LineSegment StartX=-27 StartY=-9.5 StartZ=0 EndX=-45 EndY=-9.5 EndZ=0
    g8: LineSegment StartX=-45 StartY=-9.5 StartZ=0 EndX=-45 EndY=-10.5 EndZ=0
    g9: LineSegment StartX=-45 StartY=-10.5 StartZ=0 EndX=-27 EndY=-10.5 EndZ=0
    g10: LineSegment StartX=-27 StartY=-10.5 StartZ=0 EndX=-27 EndY=-27.5 EndZ=0
    g11: LineSegment StartX=-27 StartY=-27.5 StartZ=0 EndX=-45 EndY=-27.5 EndZ=0
    g12: LineSegment StartX=-45 StartY=-27.5 StartZ=0 EndX=-45 EndY=-30 EndZ=0
    g13: LineSegment StartX=-45 StartY=-30 StartZ=0 EndX=45 EndY=-30 EndZ=0
    g14: LineSegment StartX=45 StartY=-30 StartZ=0 EndX=45 EndY=30 EndZ=0
    g15: LineSegment StartX=45 StartY=30 StartZ=0 EndX=-45 EndY=30 EndZ=0
    g16: LineSegment StartX=1.39 StartY=-21.5 StartZ=0 EndX=36.39 EndY=-21.5 EndZ=0
    g17: LineSegment StartX=36.39 StartY=-21.5 StartZ=0 EndX=36.39 EndY=-27.5 EndZ=0
    g18: LineSegment StartX=36.39 StartY=-27.5 StartZ=0 EndX=1.39 EndY=-27.5 EndZ=0
    g19: LineSegment StartX=1.39 StartY=-27.5 StartZ=0 EndX=1.39 EndY=-21.5 EndZ=0
    g20: LineSegment [constr] StartX=-45 StartY=26.25 StartZ=0 EndX=-45 EndY=9.25 EndZ=0
    g21: LineSegment [constr] StartX=-45 StartY=7.5 StartZ=0 EndX=-45 EndY=-9.5 EndZ=0
    g22: LineSegment [constr] StartX=-45 StartY=-10.5 StartZ=0 EndX=-45 EndY=-27.5 EndZ=0
    g23: LineSegment [constr] StartX=-27 StartY=-9.5 StartZ=0 EndX=-27 EndY=-10.5 EndZ=0
    g24: GeomPoint [constr] X=-45 Y=-19 Z=0
    g25: GeomPoint [constr] X=-45 Y=-1 Z=0
    g26: GeomPoint [constr] X=-45 Y=17.75 Z=0
    g27: GeomPoint [constr] X=-45 Y=28 Z=0
    g28: GeomPoint [constr] X=18.89 Y=-27.5 Z=0
    g29: GeomPoint [constr] X=36.39 Y=-24.5 Z=0
  constraints (80):
    c: Vertical(g0)
    c: Coincident(g0,g1)
    c: Horizontal(g1)
    c: Coincident(g1,g2)
    c: Vertical(g2)
    c: Coincident(g2,g3)
    c: Horizontal(g3)
    c: Coincident(g3,g4)
    c: Vertical(g4)
    c: Coincident(g4,g5)
    c: Horizontal(g5)
    c: Coincident(g5,g6)
    c: Vertical(g6)
    c: Coincident(g6,g7)
    c: Horizontal(g7)
    c: Coincident(g7,g8)
    c: Coincident(g8,g9)
    c: Horizontal(g9)
    c: Coincident(g9,g10)
    c: Vertical(g10)
    c: Coincident(g10,g11)
    c: Horizontal(g11)
    c: Coincident(g11,g12)
    c: Coincident(g12,g13)
    c: Horizontal(g13)
    c: Coincident(g13,g14)
    c: Vertical(g14)
    c: Coincident(g14,g15)
    c: Coincident(g15,g0)
    c: Horizontal(g15)
    c: Coincident(g16,g17)
    c: Coincident(g17,g18)
    c: Coincident(g18,g19)
    c: Coincident(g19,g16)
    c: Horizontal(g16)
    c: Horizontal(g18)
    c: Vertical(g17)
    c: Vertical(g19)
    c: Symmetric(g0,g14,g-2)
    c: Coincident(g20,g0)
    c: Coincident(g20,g3)
    c: Vertical(g20)
    c: Coincident(g21,g4)
    c: Coincident(g21,g7)
    c: Vertical(g21)
    c: Coincident(g22,g8)
    c: Coincident(g22,g11)
    c: Vertical(g8)
    c: Vertical(g22)
    c: Vertical(g12)
    c: Coincident(g23,g6)
    c: Coincident(g23,g9)
    c: Vertical(g23)
    c: DistanceX(g4,g5) = 18
    c: DistanceY(g3,g0) = 17
    c: DistanceY(g7,g4) = 17
    c: DistanceY(g11,g8) = 17
    c: PointOnObject(g24,g22)
    c: PointOnObject(g25,g21)
    c: PointOnObject(g26,g20)
    c: Symmetric(g3,g0,g26)
    c: Symmetric(g4,g7,g25)
    c: Symmetric(g11,g8,g24)
    c: PointOnObject(g27,g0)
    c: DistanceY(g27,g0) = 2
    c: DistanceY(g26,g27) = 10.25
    c: DistanceY(g25,g27) = 29
    c: DistanceY(g24,g27) = 47
    c: DistanceX(g0,g1) = 23
    c: Symmetric(g14,g13,g-1)
    c: DistanceX(g0,g14) = 90
    c: DistanceY(g13,g14) = 60
    c: DistanceX(g16,g16) = 35
    c: DistanceY(g18,g16) = 6
    c: PointOnObject(g28,g18)
    c: Symmetric(g18,g17,g28)
    c: DistanceX(g28,g13) = 26.11
    c: PointOnObject(g29,g17)
    c: Symmetric(g17,g16,g29)
    c: DistanceY(g13,g29) = 5.5
FEATURE [PartDesign::Pad] Pad007
  AllowMultiFace = false
  Length = 2
  Length2 = 100
  Profile = -> Sketch008
  Type = 0
FEATURE [Sketcher::SketchObject] Sketch009
  MapMode = 5
  Placement = pos=(0,0,2) rot=(0,0,1;0rad)
  Support = -> [Pad007]
  sketch-geometry (30):
    g0: LineSegment StartX=-45 StartY=9.25 StartZ=0 EndX=-43 EndY=9.25 EndZ=0
    g1: LineSegment StartX=-43 StartY=9.25 StartZ=0 EndX=-43 EndY=7.5 EndZ=0
    g2: LineSegment StartX=-43 StartY=7.5 StartZ=0 EndX=-45 EndY=7.5 EndZ=0
    g3: LineSegment StartX=-45 StartY=7.5 StartZ=0 EndX=-45 EndY=9.25 EndZ=0
    g4: LineSegment StartX=-45 StartY=-9.5 StartZ=0 EndX=-43 EndY=-9.5 EndZ=0
    g5: LineSegment StartX=-43 StartY=-9.5 StartZ=0 EndX=-43 EndY=-10.5 EndZ=0
    g6: LineSegment StartX=-43 StartY=-10.5 StartZ=0 EndX=-45 EndY=-10.5 EndZ=0
    g7: LineSegment StartX=-45 StartY=-10.5 StartZ=0 EndX=-45 EndY=-9.5 EndZ=0
    g8: LineSegment StartX=-45 StartY=-27.5 StartZ=0 EndX=-43 EndY=-27.5 EndZ=0
    g9: LineSegment StartX=-43 StartY=-27.5 StartZ=0 EndX=-43 EndY=-28.5 EndZ=0
    g10: LineSegment StartX=-43 StartY=-28.5 StartZ=0 EndX=43 EndY=-28.5 EndZ=0
    g11: LineSegment StartX=43 StartY=-28.5 StartZ=0 EndX=43 EndY=28.5 EndZ=0
    g12: LineSegment StartX=43 StartY=28.5 StartZ=0 EndX=-43 EndY=28.5 EndZ=0
    g13: LineSegment StartX=-43 StartY=28.5 StartZ=0 EndX=-43 EndY=26.25 EndZ=0
    g14: LineSegment StartX=-43 StartY=26.25 StartZ=0 EndX=-45 EndY=26.25 EndZ=0
    g15: LineSegment StartX=-45 StartY=26.25 StartZ=0 EndX=-45 EndY=30 EndZ=0
    g16: LineSegment StartX=-45 StartY=30 StartZ=0 EndX=45 EndY=30 EndZ=0
    g17: LineSegment StartX=45 StartY=30 StartZ=0 EndX=45 EndY=-30 EndZ=0
    g18: LineSegment StartX=45 StartY=-30 StartZ=0 EndX=-45 EndY=-30 EndZ=0
    g19: LineSegment StartX=-45 StartY=-30 StartZ=0 EndX=-45 EndY=-27.5 EndZ=0
    g20: LineSegment [constr] StartX=-45 StartY=-10.5 StartZ=0 EndX=-45 EndY=-27.5 EndZ=0
    g21: LineSegment [constr] StartX=-43 StartY=-27.5 StartZ=0 EndX=-43 EndY=-10.5 EndZ=0
    g22: LineSegment [constr] StartX=-45 StartY=7.5 StartZ=0 EndX=-45 EndY=-9.5 EndZ=0
    g23: LineSegment [constr] StartX=-43 StartY=7.5 StartZ=0 EndX=-43 EndY=-9.5 EndZ=0
    g24: LineSegment [constr] StartX=-45 StartY=9.25 StartZ=0 EndX=-45 EndY=26.25 EndZ=0
    g25: LineSegment [constr] StartX=-43 StartY=26.25 StartZ=0 EndX=-43 EndY=9.25 EndZ=0
    g26: GeomPoint [constr] X=-45 Y=28 Z=0
    g27: GeomPoint [constr] X=-45 Y=17.75 Z=0
    g28: GeomPoint [constr] X=-45 Y=-1 Z=0
    g29: GeomPoint [constr] X=-45 Y=-19 Z=0
  constraints (80):
    c: Coincident(g0,g1)
    c: Coincident(g1,g2)
    c: Coincident(g2,g3)
    c: Coincident(g3,g0)
    c: Horizontal(g0)
    c: Horizontal(g2)
    c: Vertical(g1)
    c: Vertical(g3)
    c: Coincident(g4,g5)
    c: Coincident(g5,g6)
    c: Coincident(g6,g7)
    c: Coincident(g7,g4)
    c: Horizontal(g4)
    c: Horizontal(g6)
    c: Vertical(g5)
    c: Vertical(g7)
    c: Coincident(g8,g9)
    c: Vertical(g9)
    c: Coincident(g9,g10)
    c: Horizontal(g10)
    c: Coincident(g10,g11)
    c: Vertical(g11)
    c: Coincident(g11,g12)
    c: Horizontal(g12)
    c: Coincident(g12,g13)
    c: Coincident(g13,g14)
    c: Horizontal(g14)
    c: Coincident(g14,g15)
    c: Vertical(g15)
    c: Coincident(g15,g16)
    c: Horizontal(g16)
    c: Coincident(g16,g17)
    c: Vertical(g17)
    c: Coincident(g17,g18)
    c: Horizontal(g18)
    c: Coincident(g18,g19)
    c: Coincident(g19,g8)
    c: Horizontal(g8)
    c: Vertical(g19)
    c: Coincident(g20,g6)
    c: Coincident(g20,g8)
    c: Vertical(g20)
    c: Coincident(g21,g8)
    c: Coincident(g21,g5)
    c: Coincident(g22,g2)
    c: Coincident(g22,g4)
    c: Vertical(g22)
    c: Coincident(g23,g1)
    c: Coincident(g23,g4)
    c: Vertical(g23)
    c: Coincident(g24,g0)
    c: Coincident(g24,g14)
    c: Vertical(g24)
    c: Coincident(g25,g13)
    c: Coincident(g25,g0)
    c: Vertical(g25)
    c: Vertical(g21)
    c: Vertical(g13)
    c: DistanceX(g8,g8) = 2
    c: Symmetric(g15,g16,g-2)
    c: Symmetric(g11,g12,g-2)
    c: Symmetric(g16,g17,g-1)
    c: Symmetric(g10,g11,g-1)
    c: DistanceX(g15,g16) = 90
    c: DistanceY(g17,g16) = 60
    c: DistanceY(g17,g10) = 1.5
    c: PointOnObject(g26,g15)
    c: DistanceY(g26,g15) = 2
    c: PointOnObject(g27,g24)
    c: PointOnObject(g28,g22)
    c: PointOnObject(g29,g20)
    c: Symmetric(g14,g0,g27)
    c: Symmetric(g4,g2,g28)
    c: Symmetric(g8,g6,g29)
    c: Equal(g25,g23)
    c: Equal(g23,g21)
    c: DistanceY(g25,g25) = 17
    c: DistanceY(g27,g26) = 10.25
    c: DistanceY(g28,g26) = 29
    c: DistanceY(g29,g26) = 47
FEATURE [PartDesign::Pad] Pad008
  AllowMultiFace = false
  Length = 9.5
  Length2 = 100
  Profile = -> Sketch009
  Type = 0
FEATURE [Sketcher::SketchObject] Sketch010
  MapMode = 5
  Placement = pos=(-45,0,0) rot=(0.57735,-0.57735,-0.57735;2.0944rad)
  Support = -> [Pad008]
  sketch-geometry (18):
    g0: LineSegment StartX=-26.25 StartY=11.5 StartZ=0 EndX=-9.25 EndY=11.5 EndZ=0
    g1: LineSegment StartX=-9.25 StartY=11.5 StartZ=0 EndX=-9.25 EndY=5 EndZ=0
    g2: LineSegment StartX=-9.25 StartY=5 StartZ=0 EndX=-26.25 EndY=5 EndZ=0
    g3: LineSegment StartX=-26.25 StartY=5 StartZ=0 EndX=-26.25 EndY=11.5 EndZ=0
    g4: LineSegment StartX=-7.5 StartY=11.5 StartZ=0 EndX=9.5 EndY=11.5 EndZ=0
    g5: LineSegment StartX=9.5 StartY=11.5 StartZ=0 EndX=9.5 EndY=7.5 EndZ=0
    g6: LineSegment StartX=9.5 StartY=7.5 StartZ=0 EndX=-7.5 EndY=7.5 EndZ=0
    g7: LineSegment StartX=-7.5 StartY=7.5 StartZ=0 EndX=-7.5 EndY=11.5 EndZ=0
    g8: LineSegment StartX=10.5 StartY=11.5 StartZ=0 EndX=27.5 EndY=11.5 EndZ=0
    g9: LineSegment StartX=27.5 StartY=11.5 StartZ=0 EndX=27.5 EndY=7.5 EndZ=0
    g10: LineSegment StartX=27.5 StartY=7.5 StartZ=0 EndX=10.5 EndY=7.5 EndZ=0
    g11: LineSegment StartX=10.5 StartY=7.5 StartZ=0 EndX=10.5 EndY=11.5 EndZ=0
    g12: LineSegment [constr] StartX=-9.25 StartY=11.5 StartZ=0 EndX=-7.5 EndY=11.5 EndZ=0
    g13: LineSegment [constr] StartX=9.5 StartY=11.5 StartZ=0 EndX=10.5 EndY=11.5 EndZ=0
    g14: GeomPoint [constr] X=-17.75 Y=5 Z=0
    g15: GeomPoint [constr] X=1 Y=7.5 Z=0
    g16: GeomPoint [constr] X=19 Y=7.5 Z=0
    g17: LineSegment [constr] StartX=9.5 StartY=7.5 StartZ=0 EndX=10.5 EndY=7.5 EndZ=0
  constraints (48):
    c: Coincident(g0,g1)
    c: Coincident(g1,g2)
    c: Coincident(g2,g3)
    c: Coincident(g3,g0)
    c: Horizontal(g0)
    c: Horizontal(g2)
    c: Vertical(g1)
    c: Vertical(g3)
    c: Coincident(g4,g5)
    c: Coincident(g5,g6)
    c: Coincident(g6,g7)
    c: Coincident(g7,g4)
    c: Horizontal(g4)
    c: Horizontal(g6)
    c: Vertical(g5)
    c: Vertical(g7)
    c: Coincident(g8,g9)
    c: Coincident(g9,g10)
    c: Coincident(g10,g11)
    c: Coincident(g11,g8)
    c: Horizontal(g8)
    c: Horizontal(g10)
    c: Vertical(g9)
    c: Vertical(g11)
    c: Coincident(g12,g0)
    c: Coincident(g12,g4)
    c: Coincident(g13,g4)
    c: Coincident(g13,g8)
    c: Horizontal(g13)
    c: Horizontal(g12)
    c: Equal(g0,g4)
    c: Equal(g4,g8)
    c: DistanceX(g0,g0) = 17
    c: PointOnObject(g14,g2)
    c: PointOnObject(g15,g6)
    c: PointOnObject(g16,g10)
    c: Symmetric(g2,g1,g14)
    c: Symmetric(g6,g5,g15)
    c: Symmetric(g10,g9,g16)
    c: DistanceX(g14,g-1) = 17.75
    c: DistanceX(g-1,g15) = 1
    c: DistanceX(g-1,g16) = 19
    c: DistanceY(g-1,g14) = 5
    c: DistanceY(g-1,g15) = 7.5
    c: Coincident(g17,g5)
    c: Coincident(g17,g10)
    c: Horizontal(g17)
    c: DistanceY(g-1,g0) = 11.5
FEATURE [PartDesign::Pad] Pad009
  AllowMultiFace = false
  Length = 2
  Length2 = 100
  Profile = -> Sketch010
  Reversed = true
  Type = 0
FEATURE [Sketcher::SketchObject] Sketch019
  MapMode = 5
  Placement = pos=(0,0,2) rot=(0,0,1;0rad)
  Support = -> [Pad009]
  sketch-geometry (34):
    g0: LineSegment StartX=-43 StartY=28.5 StartZ=0 EndX=-38 EndY=28.5 EndZ=0
    g1: LineSegment StartX=-38 StartY=28.5 StartZ=0 EndX=-38 EndY=27.5 EndZ=0
    g2: LineSegment StartX=-38 StartY=27.5 StartZ=0 EndX=-43 EndY=27.5 EndZ=0
    g3: LineSegment StartX=-43 StartY=27.5 StartZ=0 EndX=-43 EndY=28.5 EndZ=0
    g4: LineSegment StartX=-43 StartY=9.25 StartZ=0 EndX=-38 EndY=9.25 EndZ=0
    g5: LineSegment StartX=-38 StartY=9.25 StartZ=0 EndX=-38 EndY=7.5 EndZ=0
    g6: LineSegment StartX=-38 StartY=7.5 StartZ=0 EndX=-43 EndY=7.5 EndZ=0
    g7: LineSegment StartX=-43 StartY=7.5 StartZ=0 EndX=-43 EndY=9.25 EndZ=0
    g8: LineSegment StartX=-43 StartY=-9.5 StartZ=0 EndX=-38 EndY=-9.5 EndZ=0
    g9: LineSegment StartX=-38 StartY=-9.5 StartZ=0 EndX=-38 EndY=-10.5 EndZ=0
    g10: LineSegment StartX=-38 StartY=-10.5 StartZ=0 EndX=-43 EndY=-10.5 EndZ=0
    g11: LineSegment StartX=-43 StartY=-10.5 StartZ=0 EndX=-43 EndY=-9.5 EndZ=0
    g12: LineSegment StartX=-43 StartY=-27.5 StartZ=0 EndX=-38 EndY=-27.5 EndZ=0
    g13: LineSegment StartX=-38 StartY=-27.5 StartZ=0 EndX=-38 EndY=-28.5 EndZ=0
    g14: LineSegment StartX=-38 StartY=-28.5 StartZ=0 EndX=-43 EndY=-28.5 EndZ=0
    g15: LineSegment StartX=-43 StartY=-28.5 StartZ=0 EndX=-43 EndY=-27.5 EndZ=0
    g16: LineSegment StartX=38 StartY=-26.5 StartZ=0 EndX=43 EndY=-26.5 EndZ=0
    g17: LineSegment StartX=43 StartY=-26.5 StartZ=0 EndX=43 EndY=-28.5 EndZ=0
    g18: LineSegment StartX=43 StartY=-28.5 StartZ=0 EndX=38 EndY=-28.5 EndZ=0
    g19: LineSegment StartX=38 StartY=-28.5 StartZ=0 EndX=38 EndY=-26.5 EndZ=0
    g20: LineSegment StartX=38 StartY=28.5 StartZ=0 EndX=43 EndY=28.5 EndZ=0
    g21: LineSegment StartX=43 StartY=28.5 StartZ=0 EndX=43 EndY=26.5 EndZ=0
    g22: LineSegment StartX=43 StartY=26.5 StartZ=0 EndX=38 EndY=26.5 EndZ=0
    g23: LineSegment StartX=38 StartY=26.5 StartZ=0 EndX=38 EndY=28.5 EndZ=0
    g24: LineSegment [constr] StartX=-38 StartY=28.5 StartZ=0 EndX=38 EndY=28.5 EndZ=0
    g25: LineSegment [constr] StartX=38 StartY=26.5 StartZ=0 EndX=38 EndY=-26.5 EndZ=0
    g26: LineSegment [constr] StartX=43 StartY=26.5 StartZ=0 EndX=43 EndY=-26.5 EndZ=0
    g27: LineSegment [constr] StartX=-38 StartY=-28.5 StartZ=0 EndX=38 EndY=-28.5 EndZ=0
    g28: LineSegment [constr] StartX=-43 StartY=-27.5 StartZ=0 EndX=-43 EndY=-10.5 EndZ=0
    g29: LineSegment [constr] StartX=-38 StartY=-10.5 StartZ=0 EndX=-38 EndY=-27.5 EndZ=0
    g30: LineSegment [constr] StartX=-38 StartY=-9.5 StartZ=0 EndX=-38 EndY=7.5 EndZ=0
    g31: LineSegment [constr] StartX=-43 StartY=7.5 StartZ=0 EndX=-43 EndY=-9.5 EndZ=0
    g32: LineSegment [constr] StartX=-43 StartY=9.25 StartZ=0 EndX=-43 EndY=27.5 EndZ=0
    g33: LineSegment [constr] StartX=-38 StartY=27.5 StartZ=0 EndX=-38 EndY=9.25 EndZ=0
  constraints (91):
    c: Coincident(g0,g1)
    c: Coincident(g1,g2)
    c: Coincident(g2,g3)
    c: Coincident(g3,g0)
    c: Horizontal(g0)
    c: Horizontal(g2)
    c: Vertical(g1)
    c: Vertical(g3)
    c: Coincident(g4,g5)
    c: Coincident(g5,g6)
    c: Coincident(g6,g7)
    c: Coincident(g7,g4)
    c: Horizontal(g4)
    c: Horizontal(g6)
    c: Vertical(g5)
    c: Vertical(g7)
    c: Coincident(g8,g9)
    c: Coincident(g9,g10)
    c: Coincident(g10,g11)
    c: Coincident(g11,g8)
    c: Horizontal(g8)
    c: Horizontal(g10)
    c: Vertical(g9)
    c: Vertical(g11)
    c: Coincident(g12,g13)
    c: Coincident(g13,g14)
    c: Coincident(g14,g15)
    c: Coincident(g15,g12)
    c: Horizontal(g12)
    c: Horizontal(g14)
    c: Vertical(g13)
    c: Vertical(g15)
    c: Coincident(g16,g17)
    c: Coincident(g17,g18)
    c: Coincident(g18,g19)
    c: Coincident(g19,g16)
    c: Horizontal(g16)
    c: Horizontal(g18)
    c: Vertical(g17)
    c: Vertical(g19)
    c: Coincident(g20,g21)
    c: Coincident(g21,g22)
    c: Coincident(g22,g23)
    c: Coincident(g23,g20)
    c: Horizontal(g20)
    c: Horizontal(g22)
    c: Vertical(g21)
    c: Vertical(g23)
    c: Coincident(g24,g0)
    c: Coincident(g24,g20)
    c: Coincident(g25,g16)
    c: Vertical(g25)
    c: Coincident(g26,g21)
    c: Coincident(g26,g16)
    c: Vertical(g26)
    c: Coincident(g25,g22)
    c: Coincident(g27,g13)
    c: Coincident(g27,g18)
    c: Horizontal(g27)
    c: Coincident(g28,g12)
    c: Coincident(g28,g10)
    c: Coincident(g29,g9)
    c: Coincident(g29,g12)
    c: Coincident(g30,g8)
    c: Coincident(g30,g5)
    c: Vertical(g30)
    c: Coincident(g31,g6)
    c: Coincident(g31,g8)
    c: Vertical(g31)
    c: Coincident(g32,g4)
    c: Coincident(g32,g2)
    c: Vertical(g32)
    c: Coincident(g33,g1)
    c: Coincident(g33,g4)
    c: Vertical(g33)
    c: Vertical(g29)
    c: Vertical(g28)
    c: Symmetric(g0,g20,g-2)
    c: Symmetric(g0,g20,g-2)
    c: Symmetric(g16,g21,g-1)
    c: Symmetric(g20,g17,g-1)
    c: DistanceX(g0,g20) = 86
    c: DistanceY(g21,g20) = 2
    c: DistanceY(g6,g4) = 1.75
    c: DistanceY(g10,g8) = 1
    c: DistanceY(g17,g20) = 57
    c: DistanceX(g18,g17) = 5
    c: DistanceY(g8,g6) = 17
    c: Equal(g28,g31)
    c: DistanceY(g2,g0) = 1
    c: Symmetric(g2,g12,g-1)
FEATURE [PartDesign::Pad] Pad010
  AllowMultiFace = false
  Length = 4.5
  Length2 = 100
  Profile = -> Sketch019
  Type = 0
FEATURE [Sketcher::SketchObject] Sketch020
  MapMode = 5
  Placement = pos=(0,0,11.5) rot=(0,0,1;0rad)
  Support = -> [Pad010]
  sketch-geometry (4):
    g0: LineSegment StartX=-44 StartY=29 StartZ=0 EndX=44 EndY=29 EndZ=0
    g1: LineSegment StartX=44 StartY=29 StartZ=0 EndX=44 EndY=-29 EndZ=0
    g2: LineSegment StartX=44 StartY=-29 StartZ=0 EndX=-44 EndY=-29 EndZ=0
    g3: LineSegment StartX=-44 StartY=-29 StartZ=0 EndX=-44 EndY=29 EndZ=0
  constraints (12):
    c: Coincident(g0,g1)
    c: Coincident(g1,g2)
    c: Coincident(g2,g3)
    c: Coincident(g3,g0)
    c: Horizontal(g0)
    c: Horizontal(g2)
    c: Vertical(g1)
    c: Vertical(g3)
    c: Symmetric(g0,g0,g-2)
    c: DistanceX(g0,g0) = 88
    c: Symmetric(g2,g0,g-1)
    c: DistanceY(g2,g0) = 58
FEATURE [PartDesign::Pocket] Pocket001
  AllowMultiFace = false
  Length = 2
  Length2 = 100
  Profile = -> Sketch020
  Type = 0
FEATURE [Sketcher::SketchObject] Sketch021
  MapMode = 5
  Placement = pos=(0,29,0) rot=(1,0,0;1.5708rad)
  Support = -> [Pocket001]
  sketch-geometry (16):
    g0: LineSegment StartX=-32 StartY=11.5 StartZ=0 EndX=-28 EndY=11.5 EndZ=0
    g1: LineSegment StartX=-28 StartY=11.5 StartZ=0 EndX=-28 EndY=10.7 EndZ=0
    g2: LineSegment StartX=-28 StartY=10.7 StartZ=0 EndX=-32 EndY=10.7 EndZ=0
    g3: LineSegment StartX=-32 StartY=10.7 StartZ=0 EndX=-32 EndY=11.5 EndZ=0
    g4: LineSegment StartX=-2 StartY=11.5 StartZ=0 EndX=2 EndY=11.5 EndZ=0
    g5: LineSegment StartX=2 StartY=11.5 StartZ=0 EndX=2 EndY=10.7 EndZ=0
    g6: LineSegment StartX=2 StartY=10.7 StartZ=0 EndX=-2 EndY=10.7 EndZ=0
    g7: LineSegment StartX=-2 StartY=10.7 StartZ=0 EndX=-2 EndY=11.5 EndZ=0
    g8: LineSegment StartX=28 StartY=11.5 StartZ=0 EndX=32 EndY=11.5 EndZ=0
    g9: LineSegment StartX=32 StartY=11.5 StartZ=0 EndX=32 EndY=10.7 EndZ=0
    g10: LineSegment StartX=32 StartY=10.7 StartZ=0 EndX=28 EndY=10.7 EndZ=0
    g11: LineSegment StartX=28 StartY=10.7 StartZ=0 EndX=28 EndY=11.5 EndZ=0
    g12: LineSegment [constr] StartX=-28 StartY=11.5 StartZ=0 EndX=-2 EndY=11.5 EndZ=0
    g13: LineSegment [constr] StartX=2 StartY=11.5 StartZ=0 EndX=28 EndY=11.5 EndZ=0
    g14: LineSegment [constr] StartX=28 StartY=10.7 StartZ=0 EndX=2 EndY=10.7 EndZ=0
    g15: LineSegment [constr] StartX=-2 StartY=10.7 StartZ=0 EndX=-28 EndY=10.7 EndZ=0
  constraints (44):
    c: Coincident(g0,g1)
    c: Coincident(g1,g2)
    c: Coincident(g2,g3)
    c: Coincident(g3,g0)
    c: Horizontal(g0)
    c: Horizontal(g2)
    c: Vertical(g1)
    c: Vertical(g3)
    c: Coincident(g4,g5)
    c: Coincident(g5,g6)
    c: Coincident(g6,g7)
    c: Coincident(g7,g4)
    c: Horizontal(g4)
    c: Horizontal(g6)
    c: Vertical(g5)
    c: Vertical(g7)
    c: Coincident(g8,g9)
    c: Coincident(g9,g10)
    c: Coincident(g10,g11)
    c: Coincident(g11,g8)
    c: Horizontal(g8)
    c: Horizontal(g10)
    c: Vertical(g9)
    c: Vertical(g11)
    c: Coincident(g12,g0)
    c: Coincident(g12,g4)
    c: Coincident(g13,g4)
    c: Coincident(g13,g8)
    c: Horizontal(g13)
    c: Coincident(g14,g10)
    c: Coincident(g14,g5)
    c: Horizontal(g14)
    c: Coincident(g15,g6)
    c: Coincident(g15,g1)
    c: Horizontal(g15)
    c: Horizontal(g12)
    c: Equal(g0,g4)
    c: Equal(g4,g8)
    c: Equal(g12,g13)
    c: DistanceX(g4,g4) = 4
    c: DistanceX(g12,g12) = 26
    c: DistanceY(g2,g0) = 0.8
    c: Symmetric(g4,g4,g-2)
    c: DistanceY(g-1,g4) = 11.5
FEATURE [PartDesign::Pad] Pad011
  AllowMultiFace = false
  Length = 1
  Length2 = 100
  Profile = -> Sketch021
  Type = 0
FEATURE [Sketcher::SketchObject] Sketch022
  MapMode = 5
  Placement = pos=(0,-29,0) rot=(0,0.707107,0.707107;3.14159rad)
  Support = -> [Pad011]
  sketch-geometry (16):
    g0: LineSegment StartX=-32 StartY=11.5 StartZ=0 EndX=-28 EndY=11.5 EndZ=0
    g1: LineSegment StartX=-28 StartY=11.5 StartZ=0 EndX=-28 EndY=10.7 EndZ=0
    g2: LineSegment StartX=-28 StartY=10.7 StartZ=0 EndX=-32 EndY=10.7 EndZ=0
    g3: LineSegment StartX=-32 StartY=10.7 StartZ=0 EndX=-32 EndY=11.5 EndZ=0
    g4: LineSegment StartX=-2 StartY=11.5 StartZ=0 EndX=2 EndY=11.5 EndZ=0
    g5: LineSegment StartX=2 StartY=11.5 StartZ=0 EndX=2 EndY=10.7 EndZ=0
    g6: LineSegment StartX=2 StartY=10.7 StartZ=0 EndX=-2 EndY=10.7 EndZ=0
    g7: LineSegment StartX=-2 StartY=10.7 StartZ=0 EndX=-2 EndY=11.5 EndZ=0
    g8: LineSegment StartX=28 StartY=11.5 StartZ=0 EndX=32 EndY=11.5 EndZ=0
    g9: LineSegment StartX=32 StartY=11.5 StartZ=0 EndX=32 EndY=10.7 EndZ=0
    g10: LineSegment StartX=32 StartY=10.7 StartZ=0 EndX=28 EndY=10.7 EndZ=0
    g11: LineSegment StartX=28 StartY=10.7 StartZ=0 EndX=28 EndY=11.5 EndZ=0
    g12: LineSegment [constr] StartX=-28 StartY=11.5 StartZ=0 EndX=-2 EndY=11.5 EndZ=0
    g13: LineSegment [constr] StartX=2 StartY=11.5 StartZ=0 EndX=28 EndY=11.5 EndZ=0
    g14: LineSegment [constr] StartX=2 StartY=10.7 StartZ=0 EndX=28 EndY=10.7 EndZ=0
    g15: LineSegment [constr] StartX=-2 StartY=10.7 StartZ=0 EndX=-28 EndY=10.7 EndZ=0
  constraints (44):
    c: Coincident(g0,g1)
    c: Coincident(g1,g2)
    c: Coincident(g2,g3)
    c: Coincident(g3,g0)
    c: Horizontal(g0)
    c: Horizontal(g2)
    c: Vertical(g1)
    c: Vertical(g3)
    c: Coincident(g4,g5)
    c: Coincident(g5,g6)
    c: Coincident(g6,g7)
    c: Coincident(g7,g4)
    c: Horizontal(g4)
    c: Horizontal(g6)
    c: Vertical(g5)
    c: Vertical(g7)
    c: Coincident(g8,g9)
    c: Coincident(g9,g10)
    c: Coincident(g10,g11)
    c: Coincident(g11,g8)
    c: Horizontal(g8)
    c: Horizontal(g10)
    c: Vertical(g9)
    c: Vertical(g11)
    c: Coincident(g12,g0)
    c: Coincident(g12,g4)
    c: Horizontal(g12)
    c: Coincident(g13,g4)
    c: Coincident(g13,g8)
    c: Coincident(g14,g5)
    c: Coincident(g14,g10)
    c: Horizontal(g14)
    c: Coincident(g15,g6)
    c: Coincident(g15,g1)
    c: Horizontal(g15)
    c: Equal(g0,g4)
    c: Equal(g4,g8)
    c: Equal(g12,g13)
    c: Horizontal(g13)
    c: Symmetric(g4,g4,g-2)
    c: DistanceX(g4,g4) = 4
    c: DistanceX(g0,g4) = 26
    c: DistanceY(g2,g0) = 0.8
    c: DistanceY(g-1,g4) = 11.5
FEATURE [PartDesign::Pad] Pad012
  AllowMultiFace = false
  Length = 1
  Length2 = 100
  Profile = -> Sketch022
  Type = 0
FEATURE [Sketcher::SketchObject] Sketch023
  MapMode = 5
  Placement = pos=(0,0,0) rot=(1,0,0;3.14159rad)
  Support = -> [Pad012]
  sketch-geometry (22):
    g0: LineSegment StartX=36.25 StartY=31 StartZ=0 EndX=36.25 EndY=30 EndZ=0
    g1: LineSegment StartX=36.25 StartY=30 StartZ=0 EndX=38.75 EndY=30 EndZ=0
    g2: LineSegment StartX=38.75 StartY=30 StartZ=0 EndX=38.75 EndY=31 EndZ=0
    g3: LineSegment StartX=35.3101 StartY=32.6 StartZ=0 EndX=36.3101 EndY=32.6 EndZ=0
    g4: LineSegment StartX=38.6899 StartY=32.6 StartZ=0 EndX=39.6899 EndY=32.6 EndZ=0
    g5: ArcOfCircle CenterX=37.5 CenterY=32.8104 CenterZ=0 NormalX=0 NormalY=0 NormalZ=1 AngleXU=0 Radius=2.2 StartAngle=3.23737 EndAngle=4.10809
    g6: ArcOfCircle CenterX=37.5 CenterY=32.8104 CenterZ=0 NormalX=0 NormalY=0 NormalZ=1 AngleXU=0 Radius=2.2 StartAngle=5.31668 EndAngle=6.18741
    g7: LineSegment StartX=36.3101 StartY=32.6 StartZ=0 EndX=37.5 EndY=30.8104 EndZ=0
    g8: LineSegment StartX=37.5 StartY=30.8104 StartZ=0 EndX=38.6899 EndY=32.6 EndZ=0
    g9: LineSegment [constr] StartX=36.3101 StartY=32.6 StartZ=0 EndX=38.6899 EndY=32.6 EndZ=0
    g10: GeomPoint [constr] X=37.5 Y=30 Z=0
    g11: LineSegment StartX=36.25 StartY=-30 StartZ=0 EndX=36.25 EndY=-31 EndZ=0
    g12: LineSegment StartX=36.25 StartY=-30 StartZ=0 EndX=38.75 EndY=-30 EndZ=0
    g13: LineSegment StartX=38.75 StartY=-30 StartZ=0 EndX=38.75 EndY=-31 EndZ=0
    g14: ArcOfCircle CenterX=37.5 CenterY=-32.8104 CenterZ=0 NormalX=0 NormalY=0 NormalZ=1 AngleXU=0 Radius=2.2 StartAngle=2.17509 EndAngle=3.04582
    g15: ArcOfCircle CenterX=37.5 CenterY=-32.8104 CenterZ=0 NormalX=0 NormalY=0 NormalZ=1 AngleXU=0 Radius=2.2 StartAngle=0.0957767 EndAngle=0.966502
    g16: GeomPoint [constr] X=37.5 Y=-30 Z=0
    g17: LineSegment StartX=35.3101 StartY=-32.6 StartZ=0 EndX=36.3101 EndY=-32.6 EndZ=0
    g18: LineSegment StartX=39.6899 StartY=-32.6 StartZ=0 EndX=38.6899 EndY=-32.6 EndZ=0
    g19: LineSegment StartX=38.6899 StartY=-32.6 StartZ=0 EndX=37.5 EndY=-30.6 EndZ=0
    g20: LineSegment StartX=37.5 StartY=-30.6 StartZ=0 EndX=36.3101 EndY=-32.6 EndZ=0
    g21: LineSegment [constr] StartX=36.3101 StartY=-32.6 StartZ=0 EndX=38.6899 EndY=-32.6 EndZ=0
  constraints (64):
    c: Horizontal(g1)
    c: Coincident(g2,g1)
    c: Vertical(g2)
    c: Horizontal(g3)
    c: Horizontal(g4)
    c: Coincident(g5,g3)
    c: Coincident(g6,g5)
    c: Coincident(g6,g4)
    c: Coincident(g6,g2)
    c: Coincident(g0,g5)
    c: Vertical(g0)
    c: Coincident(g7,g3)
    c: Coincident(g8,g7)
    c: Coincident(g8,g4)
    c: Equal(g3,g4)
    c: Equal(g5,g6)
    c: Equal(g0,g2)
    c: Coincident(g1,g0)
    c: DistanceX(g0,g1) = 2.5
    c: DistanceY(g0,g0) = 1
    c: Equal(g7,g8)
    c: DistanceX(g3,g3) = 1
    c: Radius(g5) = 2.2
    c: Coincident(g9,g3)
    c: Coincident(g9,g4)
    c: Horizontal(g9)
    c: DistanceY(g1,g4) = 2.6
    c: DistanceY(g7,g5) = 2
    c: PointOnObject(g10,g1)
    c: Symmetric(g0,g1,g10)
    c: DistanceY(g-1,g10) = 30
    c: DistanceX(g-1,g10) = 37.5
    c: Vertical(g11)
    c: Coincident(g12,g11)
    c: Horizontal(g12)
    c: Coincident(g13,g12)
    c: Coincident(g14,g11)
    c: Coincident(g15,g14)
    c: Coincident(g15,g13)
    c: PointOnObject(g16,g12)
    c: Symmetric(g11,g12,g16)
    c: DistanceX(g12,g12) = 2.5
    c: Equal(g11,g13)
    c: DistanceY(g11,g11) = 1
    c: Vertical(g13)
    c: Equal(g15,g14)
    c: Radius(g14) = 2.2
    c: Coincident(g17,g14)
    c: Horizontal(g17)
    c: Coincident(g18,g15)
    c: Coincident(g19,g18)
    c: Coincident(g20,g19)
    c: Coincident(g20,g17)
    c: Equal(g17,g18)
    c: Horizontal(g18)
    c: DistanceX(g18,g18) = 1
    c: DistanceY(g17,g19) = 2
    c: Equal(g20,g19)
    c: DistanceY(g15,g12) = 2.6
    c: Coincident(g21,g17)
    c: Coincident(g21,g18)
    c: Horizontal(g21)
    c: DistanceY(g16,g-1) = 30
    c: DistanceX(g-1,g16) = 37.5
FEATURE [PartDesign::Pad] Pad013
  AllowMultiFace = false
  Length = 9.5
  Length2 = 100
  Profile = -> Sketch023
  Reversed = true
  Type = 0
FEATURE [PartDesign::LinearPattern] LinearPattern001
  Direction = -> Sketch023 [H_Axis]
  Length = 75
  Occurrences = 6
  Originals = -> [Pad013]
  Reversed = true
FEATURE [PartDesign::Chamfer] Chamfer010
  Base = -> LinearPattern001 [Edge581,Edge577,Edge584,Edge557,Edge560,Edge563]
  Size = 0.2
  SupportTransform = false
FEATURE [Part::Cut] Cut028
  Base = -> Chamfer010
  Tool = -> Fusion074
FEATURE [Part::Cut] Cut029  label="Bottom v4 with ribbon slot raw001"
  Base = -> Cut028
  Tool = -> Fusion073
FEATURE [Part::Chamfer] Chamfer008
  Base = -> Cut029
  Edges = 1 edges r=1.9: [Edge708]
FEATURE [Part::Chamfer] Chamfer009  label="Bottom v4 with ribbon slot001"
  Base = -> Chamfer008
  Edges = 1 edges r=1.9: [Edge57]
FEATURE [Part::Box] Box076  label="Würfel050"
  AttacherType = Attacher::AttachEngine3D
  Height = 9
  Length = 2
  Placement = pos=(-45,-30,0) rot=(0,0,1;0rad)
  Width = 60
FEATURE [Part::Box] Box077  label="Würfel051"
  AttacherType = Attacher::AttachEngine3D
  Height = 2
  Length = 25
  Placement = pos=(-45,-30,0) rot=(0,0,1;0rad)
  Width = 60
FEATURE [Part::MultiFuse] Fusion072
  Shapes = -> [Box077,Box076]
FEATURE [Part::MultiFuse] Fusion071  label="DisplayBottom without slots"
  Placement = pos=(0,0,0) rot=(0,0,1;3.14159rad)
  Shapes = -> [Chamfer009,Fusion072]
FEATURE [Part::Cut] Cut030
  Base = -> Fusion071
  Placement = pos=(0,0,14.75) rot=(0,0,1;0rad)
  Tool = -> Fusion056
FEATURE [Part::Box] Box078  label="Würfel052"
  AttacherType = Attacher::AttachEngine3D
  Height = 5
  Length = 10
  Placement = pos=(33,5,19) rot=(0,0,1;0rad)
  Width = 10
FEATURE [Part::Cut] Cut031
  Base = -> Cut030
  Tool = -> Box078
FEATURE [Part::Box] Box079  label="Würfel053"
  AttacherType = Attacher::AttachEngine3D
  Height = 6.25
  Length = 6
  Placement = pos=(38,-12,15) rot=(0,0,1;0rad)
  Width = 4
FEATURE [Part::Box] Box080  label="Würfel054"
  AttacherType = Attacher::AttachEngine3D
  Height = 6.25
  Length = 6
  Placement = pos=(38,6,15) rot=(0,0,1;0rad)
  Width = 3.4
FEATURE [Part::MultiFuse] Fusion075  label="Display-Wanne v4 / TX-Pi4"
  Shapes = -> [Box079,Box080,Cut031]
FEATURE [Part::Box] Box081  label="Würfel055"
  AttacherType = Attacher::AttachEngine3D
  Height = 1
  Length = 10
  Placement = pos=(-15,16.5,14.75) rot=(0,0,1;0rad)
  Width = 10
FEATURE [Part::Box] Box082  label="Würfel056"
  AttacherType = Attacher::AttachEngine3D
  Height = 1
  Length = 56
  Placement = pos=(-38,19.5,14.75) rot=(0,0,1;0rad)
  Width = 10
FEATURE [Part::Box] Box083  label="Würfel057"
  AttacherType = Attacher::AttachEngine3D
  Height = 1
  Length = 5
  Placement = pos=(-12.5,18.25,12.75) rot=(0,0,1;0rad)
  Width = 1
FEATURE [Part::Box] Box084  label="Würfel058"
  AttacherType = Attacher::AttachEngine3D
  Height = 2.2
  Length = 5
  Placement = pos=(-12.5,19.25,12.55) rot=(0,0,1;0rad)
  Width = 1
FEATURE [Part::Chamfer] Chamfer011
  Base = -> Box083
  Edges = 2 edges r=0.49: [Edge9,Edge10]
  Placement = pos=(0,0,-0.2) rot=(0,0,1;0rad)
FEATURE [Part::Chamfer] Chamfer012
  Base = -> Box084
  Edges = 1 edges r=0.9: [Edge11]
FEATURE [Part::MultiFuse] Fusion076  label="Nase"
  Shapes = -> [Chamfer012,Chamfer011]
FEATURE [Part::MultiFuse] Fusion077  label="Deckl"
  Shapes = -> [Box081,Box082]
FEATURE [Part::Box] Box085  label="Würfel059"
  AttacherType = Attacher::AttachEngine3D
  Height = 1
  Length = 5
  Placement = pos=(-12.5,18.25,12.75) rot=(0,0,1;0rad)
  Width = 1
FEATURE [Part::Chamfer] Chamfer013
  Base = -> Box085
  Edges = 2 edges r=0.49: [Edge9,Edge10]
  Placement = pos=(0,0,-0.2) rot=(0,0,1;0rad)
FEATURE [Part::Box] Box086  label="Würfel060"
  AttacherType = Attacher::AttachEngine3D
  Height = 2.2
  Length = 5
  Placement = pos=(-12.5,19.25,12.55) rot=(0,0,1;0rad)
  Width = 1
FEATURE [Part::Chamfer] Chamfer014
  Base = -> Box086
  Edges = 1 edges r=0.9: [Edge11]
FEATURE [Part::MultiFuse] Fusion078  label="Nase001"
  Placement = pos=(1,47,0) rot=(0,0,1;3.14159rad)
  Shapes = -> [Chamfer014,Chamfer013]
FEATURE [Part::Box] Box087  label="Würfel061"
  AttacherType = Attacher::AttachEngine3D
  Height = 2.2
  Length = 5
  Placement = pos=(-12.5,19.25,12.55) rot=(0,0,1;0rad)
  Width = 1
FEATURE [Part::Box] Box088  label="Würfel062"
  AttacherType = Attacher::AttachEngine3D
  Height = 1
  Length = 5
  Placement = pos=(-12.5,18.25,12.75) rot=(0,0,1;0rad)
  Width = 1
FEATURE [Part::Chamfer] Chamfer015
  Base = -> Box088
  Edges = 2 edges r=0.49: [Edge9,Edge10]
  Placement = pos=(0,0,-0.2) rot=(0,0,1;0rad)
FEATURE [Part::Chamfer] Chamfer016
  Base = -> Box087
  Edges = 1 edges r=0.9: [Edge11]
FEATURE [Part::MultiFuse] Fusion079  label="Nase002"
  Placement = pos=(-42,47,0) rot=(0,0,1;3.14159rad)
  Shapes = -> [Chamfer016,Chamfer015]
FEATURE [Part::MultiFuse] Fusion080  label="Nasen"
  Shapes = -> [Fusion076,Fusion078,Fusion079]
FEATURE [Part::MultiFuse] Fusion081  label="Abdeckung GPIO"
  Shapes = -> [Fusion080,Fusion077]
